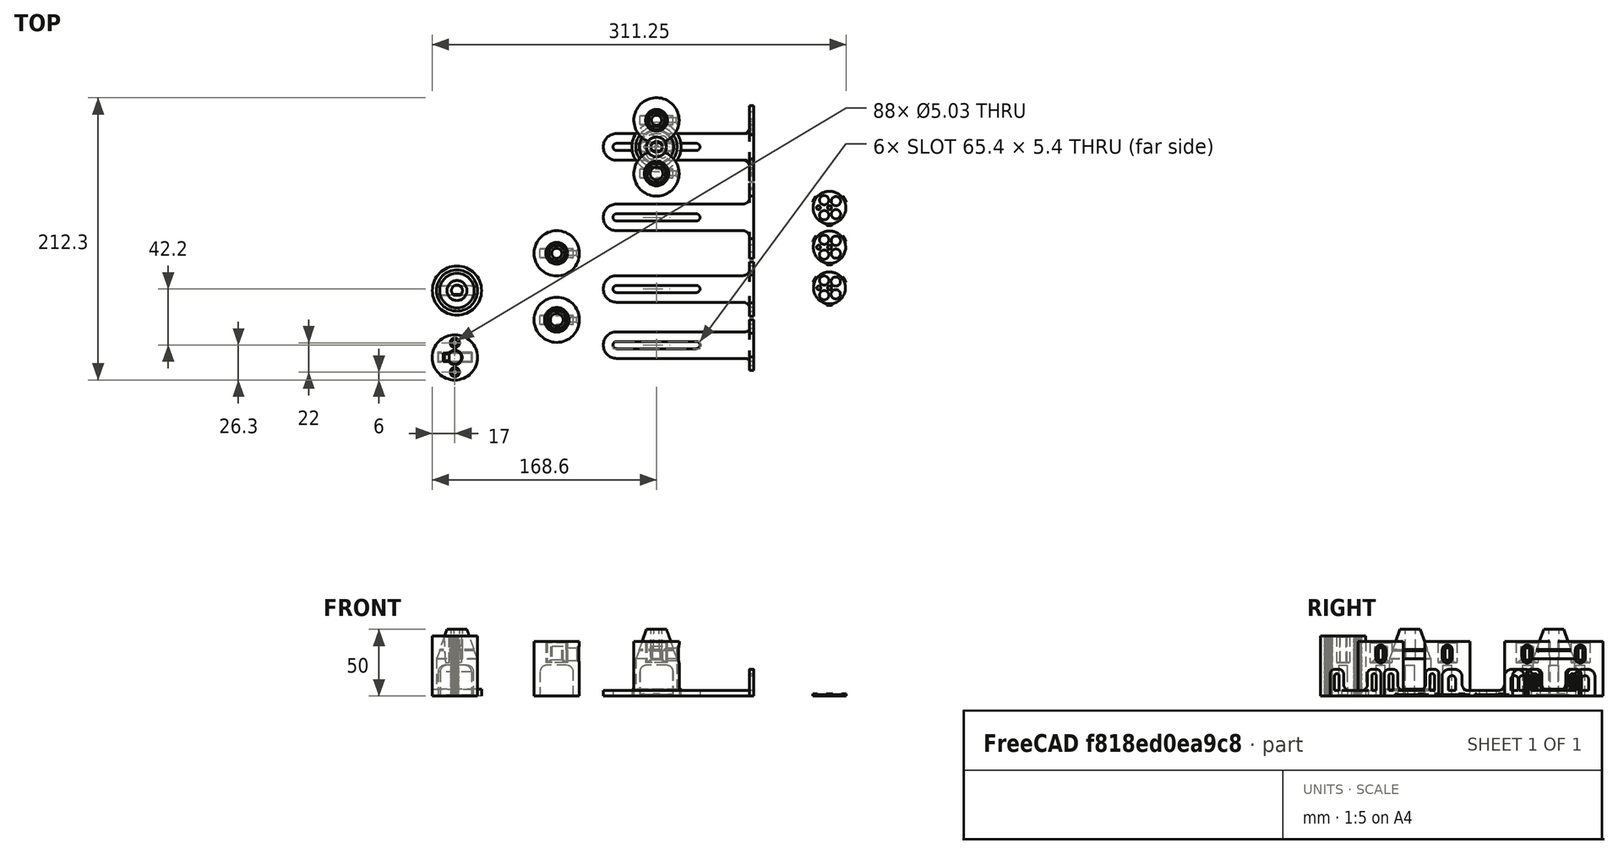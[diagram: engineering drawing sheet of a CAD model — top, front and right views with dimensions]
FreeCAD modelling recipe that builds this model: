
FCSTD DOCUMENT  (FreeCAD 1.0R39285 (Git))
Label: Scherenheberwellenkupplungsadapter
License: All rights reserved
LicenseURL: https://en.wikipedia.org/wiki/All_rights_reserved
objects: Sketcher::SketchObject×41, PartDesign::Pad×23, Part::Feature×12, Mesh::Feature×12, PartDesign::Body×11, PartDesign::Pocket×7, PartDesign::Chamfer×5, App::DocumentObjectGroup×4, PartDesign::AdditiveLoft×3, PartDesign::Plane×2, Measure::MeasureDistance×1, PartDesign::SubtractiveLoft×1, PartDesign::Hole×1
note: 227 computed .brp shape members not serialized (recipe doc carries the construction recipe); baked Part::Feature solids carry a one-line shape summary decoded from their .brp

FEATURE [Sketcher::SketchObject] Sketch  label="Sk-Kupplungszylinder 8x14"
  ArcFitTolerance = 1e-06
  AttachmentSupport = -> [XY_Plane]
  FullyConstrained = true
  MakeInternals = false
  MapMode = 5
  sketch-geometry (1):
    g0: Circle CenterX=0 CenterY=0 CenterZ=0 NormalX=0 NormalY=0 NormalZ=1 AngleXU=0 Radius=17
  constraints (2):
    c: Diameter(g0) = 34
    c: Coincident(g0,g-1)
FEATURE [PartDesign::Pad] Pad  label="P-Kupplungszylinder 8x14"
  Direction = (0,0,1)
  Length = 25
  Length2 = 10
  Profile = -> Sketch
  ReferenceAxis = -> Sketch [N_Axis]
  Refine = true
  Suppressed = false
  Type = 0
FEATURE [Sketcher::SketchObject] Sketch001  label="Sk-Konus groß 8x14"
  ArcFitTolerance = 1e-06
  AttachmentSupport = -> [Pad]
  FullyConstrained = true
  MakeInternals = false
  MapMode = 5
  Placement = pos=(0,0,25) rot=(0,0,1;0rad)
  sketch-geometry (1):
    g0: Circle CenterX=0 CenterY=0 CenterZ=0 NormalX=0 NormalY=0 NormalZ=1 AngleXU=0 Radius=6
  constraints (2):
    c: Coincident(g0,g-1)
    c: Diameter(g0) = 12
FEATURE [Sketcher::SketchObject] Sketch002  label="Sk-Konus klein 8x14"
  ArcFitTolerance = 1e-06
  AttachmentOffset = pos=(0,0,2) rot=(0,0,1;0rad)
  AttachmentSupport = -> [Pad]
  FullyConstrained = true
  MakeInternals = false
  MapMode = 5
  Placement = pos=(0,0,27) rot=(0,0,1;0rad)
  sketch-geometry (1):
    g0: Circle CenterX=0 CenterY=0 CenterZ=0 NormalX=0 NormalY=0 NormalZ=1 AngleXU=0 Radius=3.8
  constraints (2):
    c: Diameter(g0) = 7.6
    c: Coincident(g0,g-1)
FEATURE [PartDesign::AdditiveLoft] AdditiveLoft  label="P-mit Konus 8x14"
  BaseFeature = -> Pad
  Closed = true
  Profile = -> Sketch001
  Refine = true
  Ruled = true
  Sections = -> [Sketch002]
  Suppressed = false
FEATURE [Sketcher::SketchObject] Sketch003  label="Sk-Innenbolzen 8x14"
  ArcFitTolerance = 1e-06
  AttachmentSupport = -> [AdditiveLoft]
  ExternalGeometry = -> [AdditiveLoft]
  FullyConstrained = true
  MakeInternals = false
  MapMode = 5
  Placement = pos=(0,0,27) rot=(0,0,1;0rad)
  sketch-geometry (1):
    g0: Circle CenterX=0 CenterY=0 CenterZ=0 NormalX=0 NormalY=0 NormalZ=1 AngleXU=0 Radius=3.8
  constraints (2):
    c: Coincident(g0,g-1)
    c: Equal(g-3,g0)
FEATURE [PartDesign::Pad] Pad001  label="P-Innenbolzen 8x14"
  BaseFeature = -> AdditiveLoft
  Direction = (0,0,1)
  Length = 10
  Length2 = 10
  Profile = -> Sketch003
  ReferenceAxis = -> Sketch003 [N_Axis]
  Refine = true
  Suppressed = false
  Type = 0
FEATURE [Sketcher::SketchObject] Sketch004  label="Sk-Kupplungsrohr 8x14"
  ArcFitTolerance = 1e-06
  AttachmentSupport = -> [Pad001]
  ExternalGeometry = -> [Pad001]
  FullyConstrained = true
  MakeInternals = false
  MapMode = 5
  Placement = pos=(0,0,37) rot=(0,0,1;0rad)
  sketch-geometry (2):
    g0: Circle CenterX=0 CenterY=0 CenterZ=0 NormalX=0 NormalY=0 NormalZ=1 AngleXU=0 Radius=17
    g1: Circle CenterX=0 CenterY=0 CenterZ=0 NormalX=0 NormalY=0 NormalZ=1 AngleXU=0 Radius=7.2
  constraints (4):
    c: Coincident(g0,g-1)
    c: Equal(g0,g-3)
    c: Diameter(g1) = 14.4
    c: Coincident(g1,g0)
FEATURE [PartDesign::Pad] Pad002  label="P-Adapterhülle 8x14"
  BaseFeature = -> Pad001
  Direction = (0,0,1)
  Length = 4
  Length2 = 14
  Profile = -> Sketch004
  ReferenceAxis = -> Sketch004 [N_Axis]
  Refine = true
  Suppressed = false
  Type = 4
FEATURE [Sketcher::SketchObject] Sketch005  label="Sk-Spindelnut 8x14"
  ArcFitTolerance = 1e-06
  AttachmentSupport = -> [XZ_Plane]
  FullyConstrained = true
  MakeInternals = false
  MapMode = 5
  Placement = pos=(0,0,0) rot=(1,0,0;1.5708rad)
  sketch-geometry (8):
    g0: LineSegment StartX=-12.5 StartY=0 StartZ=0 EndX=12.5 EndY=0 EndZ=0
    g1: LineSegment StartX=12.5 StartY=0 StartZ=0 EndX=12.5 EndY=18 EndZ=0
    g2: LineSegment StartX=7.5 StartY=23 StartZ=0 EndX=-7.5 EndY=23 EndZ=0
    g3: LineSegment StartX=-12.5 StartY=18 StartZ=0 EndX=-12.5 EndY=0 EndZ=0
    g4: ArcOfCircle CenterX=-7.5 CenterY=18 CenterZ=0 NormalX=0 NormalY=0 NormalZ=1 AngleXU=0 Radius=5 StartAngle=1.5708 EndAngle=3.14159
    g5: GeomPoint [constr] X=-12.5 Y=23 Z=0
    g6: ArcOfCircle CenterX=7.5 CenterY=18 CenterZ=0 NormalX=0 NormalY=0 NormalZ=1 AngleXU=0 Radius=5 StartAngle=1e-16 EndAngle=1.5708
    g7: GeomPoint [constr] X=12.5 Y=23 Z=0
  constraints (19):
    c: Coincident(g0,g1)
    c: Coincident(g3,g0)
    c: Horizontal(g2)
    c: Vertical(g1)
    c: Vertical(g3)
    c: DistanceX(g5,g7) = 25
    c: DistanceY(g1,g7) = 23
    c: PointOnObject(g5,g3)
    c: PointOnObject(g5,g2)
    c: Tangent(g3,g4) = -1.5708
    c: Tangent(g2,g4) = -1.5708
    c: PointOnObject(g7,g2)
    c: PointOnObject(g7,g1)
    c: Tangent(g2,g6) = -1.5708
    c: Tangent(g1,g6) = -1.5708
    c: Equal(g4,g6)
    c: Radius(g4) = 5
    c: Symmetric(g0,g0,g-2)
    c: PointOnObject(g0,g-1)
FEATURE [PartDesign::Pocket] Pocket  label="P-Adapter mit  Nut 8x14"
  BaseFeature = -> Pad002
  Direction = (0,1,-2e-16)
  Length = 6.6
  Length2 = 5
  Midplane = true
  Profile = -> Sketch005
  ReferenceAxis = -> Sketch005 [N_Axis]
  Refine = true
  Suppressed = false
  Type = 0
FEATURE [PartDesign::Plane] DatumPlane  label="DatumPlane 8x14"
  AttachmentSupport = -> [Pocket]
  Length = 61.4891
  MapMode = 6
  Placement = pos=(17,0,41) rot=(0.57735,0.57735,0.57735;2.0944rad)
  ResizeMode = 0
  Width = 77.4891
FEATURE [Sketcher::SketchObject] Sketch006  label="Sk-Kupplungsbohrung 8x14"
  ArcFitTolerance = 1e-06
  AttachmentSupport = -> [DatumPlane]
  FullyConstrained = true
  MakeInternals = false
  MapMode = 5
  Placement = pos=(17,0,41) rot=(0.57735,0.57735,0.57735;2.0944rad)
  sketch-geometry (5):
    g0: LineSegment [constr] StartX=0 StartY=0 StartZ=0 EndX=0 EndY=-6.5 EndZ=0
    g1: ArcOfCircle CenterX=-1e-16 CenterY=-12.5 CenterZ=0 NormalX=0 NormalY=0 NormalZ=1 AngleXU=0 Radius=1.8 StartAngle=3.14159 EndAngle=6.28319
    g2: ArcOfCircle CenterX=0 CenterY=-6.5 CenterZ=0 NormalX=0 NormalY=0 NormalZ=1 AngleXU=0 Radius=1.8 StartAngle=0 EndAngle=3.14159
    g3: LineSegment StartX=-1.8 StartY=-6.5 StartZ=0 EndX=-1.8 EndY=-12.5 EndZ=0
    g4: LineSegment StartX=1.8 StartY=-6.5 StartZ=0 EndX=1.8 EndY=-12.5 EndZ=0
  constraints (12):
    c: Distance(g0) = 6.5
    c: Vertical(g0)
    c: Diameter(g1) = 3.6
    c: Vertical(g3)
    c: Vertical(g4)
    c: Tangent(g3,g2) = -1.5708
    c: Tangent(g4,g1) = 1.5708
    c: Tangent(g3,g1) = -1.5708
    c: Coincident(g2,g0)
    c: Tangent(g4,g2) = 1.5708
    c: Coincident(g0,g-1)
    c: DistanceY(g1,g0) = 6
FEATURE [PartDesign::Pocket] Pocket001  label="P-Scherenheberkupplungsadapter 8x14 roh"
  BaseFeature = -> Pocket
  Direction = (-1,0,0)
  Length = 10
  Length2 = 5
  Profile = -> Sketch006
  ReferenceAxis = -> Sketch006 [N_Axis]
  Refine = true
  Suppressed = false
  Type = 0
FEATURE [PartDesign::Chamfer] Chamfer  label="P-Scherenheberkupplungsadapter 8x14 gefast"
  Angle = 45
  Base = -> Pocket001 [Edge40]
  BaseFeature = -> Pocket001
  ChamferType = 0
  FlipDirection = false
  Refine = true
  Size = 1
  Size2 = 1
  SupportTransform = false
  Suppressed = false
  UseAllEdges = false
FEATURE [PartDesign::Chamfer] Chamfer001  label="P-Scherenheberkupplungsadapter 8x14"
  Angle = 45
  Base = -> Chamfer [Edge8,Edge10,Edge11,Edge12,Edge6,Edge7]
  BaseFeature = -> Chamfer
  ChamferType = 0
  FlipDirection = false
  Refine = true
  Size = 2
  Size2 = 1
  SupportTransform = false
  Suppressed = false
  UseAllEdges = false
FEATURE [PartDesign::Body] Body  label="B-Scherenheberkupplungsadpter-8x14mm"
  AllowCompound = false
  Group = -> [Sketch,Pad,Sketch001,Sketch002,AdditiveLoft,Sketch003,Pad001,Sketch004,Pad002,Sketch005,Pocket,DatumPlane,Sketch006,Pocket001,Chamfer,Chamfer001]
  Origin = -> Origin
  Placement = pos=(-75,-80,0) rot=(0,0,1;0rad)
  Tip = -> Chamfer001
FEATURE [Sketcher::SketchObject] Sketch007  label="Sk-Kupplungszylinder 10x16"
  ArcFitTolerance = 1e-06
  AttachmentSupport = -> [XY_Plane001]
  FullyConstrained = true
  MakeInternals = false
  MapMode = 5
  sketch-geometry (1):
    g0: Circle CenterX=0 CenterY=0 CenterZ=0 NormalX=0 NormalY=0 NormalZ=1 AngleXU=0 Radius=17
  constraints (2):
    c: Diameter(g0) = 34
    c: Coincident(g0,g-1)
FEATURE [PartDesign::Pad] Pad003  label="P-Kupplungszylinder 10x16"
  Direction = (0,0,1)
  Length = 25
  Length2 = 10
  Profile = -> Sketch007
  ReferenceAxis = -> Sketch007 [N_Axis]
  Refine = true
  Suppressed = false
  Type = 0
FEATURE [Sketcher::SketchObject] Sketch008  label="Sk-Konus groß  10x16"
  ArcFitTolerance = 1e-06
  AttachmentSupport = -> [Pad003]
  FullyConstrained = true
  MakeInternals = false
  MapMode = 5
  Placement = pos=(0,0,25) rot=(0,0,1;0rad)
  sketch-geometry (1):
    g0: Circle CenterX=0 CenterY=0 CenterZ=0 NormalX=0 NormalY=0 NormalZ=1 AngleXU=0 Radius=7
  constraints (2):
    c: Coincident(g0,g-1)
    c: Diameter(g0) = 14
FEATURE [Sketcher::SketchObject] Sketch009  label="Sk-Konus klein 10x16"
  ArcFitTolerance = 1e-06
  AttachmentOffset = pos=(0,0,2) rot=(0,0,1;0rad)
  AttachmentSupport = -> [Pad003]
  FullyConstrained = true
  MakeInternals = false
  MapMode = 5
  Placement = pos=(0,0,27) rot=(0,0,1;0rad)
  sketch-geometry (1):
    g0: Circle CenterX=0 CenterY=0 CenterZ=0 NormalX=0 NormalY=0 NormalZ=1 AngleXU=0 Radius=4.8
  constraints (2):
    c: Diameter(g0) = 9.6
    c: Coincident(g0,g-1)
FEATURE [PartDesign::AdditiveLoft] AdditiveLoft001  label="P-mit Konus  10x16"
  BaseFeature = -> Pad003
  Closed = true
  Profile = -> Sketch008
  Refine = true
  Ruled = true
  Sections = -> [Sketch009]
  Suppressed = false
FEATURE [Sketcher::SketchObject] Sketch010  label="Sk-Innenbolzen 10x16"
  ArcFitTolerance = 1e-06
  AttachmentSupport = -> [AdditiveLoft001]
  ExternalGeometry = -> [AdditiveLoft001]
  FullyConstrained = true
  MakeInternals = false
  MapMode = 5
  Placement = pos=(0,0,27) rot=(0,0,1;0rad)
  sketch-geometry (1):
    g0: Circle CenterX=0 CenterY=0 CenterZ=0 NormalX=0 NormalY=0 NormalZ=1 AngleXU=0 Radius=4.8
  constraints (2):
    c: Coincident(g0,g-1)
    c: Equal(g-3,g0)
FEATURE [PartDesign::Pad] Pad004  label="P-Innenbolzen 10x16"
  BaseFeature = -> AdditiveLoft001
  Direction = (0,0,1)
  Length = 10
  Length2 = 10
  Profile = -> Sketch010
  ReferenceAxis = -> Sketch010 [N_Axis]
  Refine = true
  Suppressed = false
  Type = 0
FEATURE [Sketcher::SketchObject] Sketch011  label="Sk-Kupplungsrohr 10x16"
  ArcFitTolerance = 1e-06
  AttachmentSupport = -> [Pad004]
  ExternalGeometry = -> [Pad004]
  FullyConstrained = true
  MakeInternals = false
  MapMode = 5
  Placement = pos=(0,0,37) rot=(0,0,1;0rad)
  sketch-geometry (2):
    g0: Circle CenterX=0 CenterY=0 CenterZ=0 NormalX=0 NormalY=0 NormalZ=1 AngleXU=0 Radius=17
    g1: Circle CenterX=0 CenterY=0 CenterZ=0 NormalX=0 NormalY=0 NormalZ=1 AngleXU=0 Radius=8.2
  constraints (4):
    c: Coincident(g0,g-1)
    c: Equal(g0,g-3)
    c: Diameter(g1) = 16.4
    c: Coincident(g1,g0)
FEATURE [PartDesign::Pad] Pad005  label="P-Adapterhülle 10x16"
  BaseFeature = -> Pad004
  Direction = (0,0,1)
  Length = 4
  Length2 = 14
  Profile = -> Sketch011
  ReferenceAxis = -> Sketch011 [N_Axis]
  Refine = true
  Suppressed = false
  Type = 4
FEATURE [Sketcher::SketchObject] Sketch012  label="Sk-Spindelnut 10x16"
  ArcFitTolerance = 1e-06
  AttachmentSupport = -> [XZ_Plane001]
  FullyConstrained = true
  MakeInternals = false
  MapMode = 5
  Placement = pos=(0,0,0) rot=(1,0,0;1.5708rad)
  sketch-geometry (8):
    g0: LineSegment StartX=-12.5 StartY=0 StartZ=0 EndX=12.5 EndY=0 EndZ=0
    g1: LineSegment StartX=12.5 StartY=0 StartZ=0 EndX=12.5 EndY=18 EndZ=0
    g2: LineSegment StartX=7.5 StartY=23 StartZ=0 EndX=-7.5 EndY=23 EndZ=0
    g3: LineSegment StartX=-12.5 StartY=18 StartZ=0 EndX=-12.5 EndY=0 EndZ=0
    g4: ArcOfCircle CenterX=-7.5 CenterY=18 CenterZ=0 NormalX=0 NormalY=0 NormalZ=1 AngleXU=0 Radius=5 StartAngle=1.5708 EndAngle=3.14159
    g5: GeomPoint [constr] X=-12.5 Y=23 Z=0
    g6: ArcOfCircle CenterX=7.5 CenterY=18 CenterZ=0 NormalX=0 NormalY=0 NormalZ=1 AngleXU=0 Radius=5 StartAngle=1e-16 EndAngle=1.5708
    g7: GeomPoint [constr] X=12.5 Y=23 Z=0
  constraints (19):
    c: Coincident(g0,g1)
    c: Coincident(g3,g0)
    c: Horizontal(g2)
    c: Vertical(g1)
    c: Vertical(g3)
    c: DistanceX(g5,g7) = 25
    c: DistanceY(g1,g7) = 23
    c: PointOnObject(g5,g3)
    c: PointOnObject(g5,g2)
    c: Tangent(g3,g4) = -1.5708
    c: Tangent(g2,g4) = -1.5708
    c: PointOnObject(g7,g2)
    c: PointOnObject(g7,g1)
    c: Tangent(g2,g6) = -1.5708
    c: Tangent(g1,g6) = -1.5708
    c: Equal(g4,g6)
    c: Radius(g4) = 5
    c: Symmetric(g0,g0,g-2)
    c: PointOnObject(g0,g-1)
FEATURE [PartDesign::Pocket] Pocket002  label="P-Adapter mit  Nut 10x16"
  BaseFeature = -> Pad005
  Direction = (0,1,-2e-16)
  Length = 6.6
  Length2 = 5
  Midplane = true
  Profile = -> Sketch012
  ReferenceAxis = -> Sketch012 [N_Axis]
  Refine = true
  Suppressed = false
  Type = 0
FEATURE [PartDesign::Plane] DatumPlane001  label="DatumPlane 10x16"
  AttachmentSupport = -> [Pocket002]
  Length = 61.4891
  MapMode = 6
  Placement = pos=(17,0,41) rot=(0.57735,0.57735,0.57735;2.0944rad)
  ResizeMode = 0
  Width = 77.4891
FEATURE [Sketcher::SketchObject] Sketch013  label="Sk-Kupplungsbohrung 10x16"
  ArcFitTolerance = 1e-06
  AttachmentSupport = -> [DatumPlane001]
  FullyConstrained = true
  MakeInternals = false
  MapMode = 5
  Placement = pos=(17,0,41) rot=(0.57735,0.57735,0.57735;2.0944rad)
  sketch-geometry (5):
    g0: LineSegment [constr] StartX=0 StartY=0 StartZ=0 EndX=0 EndY=-6.5 EndZ=0
    g1: ArcOfCircle CenterX=-1e-16 CenterY=-12.5 CenterZ=0 NormalX=0 NormalY=0 NormalZ=1 AngleXU=0 Radius=1.8 StartAngle=3.14159 EndAngle=6.28319
    g2: ArcOfCircle CenterX=0 CenterY=-6.5 CenterZ=0 NormalX=0 NormalY=0 NormalZ=1 AngleXU=0 Radius=1.8 StartAngle=0 EndAngle=3.14159
    g3: LineSegment StartX=-1.8 StartY=-6.5 StartZ=0 EndX=-1.8 EndY=-12.5 EndZ=0
    g4: LineSegment StartX=1.8 StartY=-6.5 StartZ=0 EndX=1.8 EndY=-12.5 EndZ=0
  constraints (12):
    c: Distance(g0) = 6.5
    c: Vertical(g0)
    c: Diameter(g1) = 3.6
    c: Vertical(g3)
    c: Vertical(g4)
    c: Tangent(g3,g2) = -1.5708
    c: Tangent(g4,g1) = 1.5708
    c: Tangent(g3,g1) = -1.5708
    c: Coincident(g2,g0)
    c: Tangent(g4,g2) = 1.5708
    c: Coincident(g0,g-1)
    c: DistanceY(g1,g0) = 6
FEATURE [PartDesign::Pocket] Pocket003  label="P-Scherenheberkupplungsadapter  10x16 roh"
  BaseFeature = -> Pocket002
  Direction = (-1,0,0)
  Length = 10
  Length2 = 5
  Profile = -> Sketch013
  ReferenceAxis = -> Sketch013 [N_Axis]
  Refine = true
  Suppressed = false
  Type = 0
FEATURE [PartDesign::Chamfer] Chamfer002  label="P-Scherenheberkupplungsadapter 10x16 gefast"
  Angle = 45
  Base = -> Pocket003 [Edge36]
  BaseFeature = -> Pocket003
  ChamferType = 0
  FlipDirection = false
  Refine = true
  Size = 1
  Size2 = 1
  SupportTransform = false
  Suppressed = false
  UseAllEdges = false
FEATURE [PartDesign::Chamfer] Chamfer003  label="P-Scherenheberkupplungsadapter 10x16"
  Angle = 45
  Base = -> Chamfer002 [Edge8,Edge10,Edge11,Edge12,Edge6,Edge7]
  BaseFeature = -> Chamfer002
  ChamferType = 0
  FlipDirection = false
  Refine = true
  Size = 2
  Size2 = 1
  SupportTransform = false
  Suppressed = false
  UseAllEdges = false
FEATURE [PartDesign::Body] Body001  label="B-Scherenheberkupplungsadpter-10x16mm"
  AllowCompound = false
  Group = -> [Sketch007,Pad003,Sketch008,Sketch009,AdditiveLoft001,Sketch010,Pad004,Sketch011,Pad005,Sketch012,Pocket002,DatumPlane001,Sketch013,Pocket003,Chamfer002,Chamfer003]
  Origin = -> Origin001
  Placement = pos=(-75,-130,0) rot=(0,0,1;0rad)
  Tip = -> Chamfer003
FEATURE [Part::Feature] Body002  label="S-Scherenheberkupplungsadpter-10x16mm"
  Placement = pos=(0,-20,0) rot=(0,0,1;0rad)
  shape: bbox 34 x 34 x 41 mm, 26 faces (baked)
FEATURE [Part::Feature] Body003  label="S-Scherenheberkupplungsadpter-8x14mm"
  Placement = pos=(0,20,0) rot=(0,0,1;0rad)
  shape: bbox 34 x 34 x 41 mm, 28 faces (baked)
FEATURE [Mesh::Feature] Mesh  label="M-Scherenheberkupplungsadpter-10x16mm"
FEATURE [Mesh::Feature] Mesh001  label="M-Scherenheberkupplungsadpter-08x14mm"
FEATURE [Sketcher::SketchObject] Sketch014  label="B-Montagewinkel NEMA23 - Strebe"
  ArcFitTolerance = 1e-06
  AttachmentSupport = -> [XY_Plane002]
  FullyConstrained = true
  MakeInternals = false
  MapMode = 5
  sketch-geometry (21):
    g0: ArcOfCircle CenterX=-30 CenterY=7.88454e-11 CenterZ=0 NormalX=0 NormalY=0 NormalZ=1 AngleXU=0 Radius=10 StartAngle=1.5708 EndAngle=4.71239
    g1: LineSegment StartX=-30 StartY=-10 StartZ=0 EndX=65 EndY=-10 EndZ=0
    g2: LineSegment StartX=-30 StartY=10 StartZ=0 EndX=65 EndY=10 EndZ=0
    g3: LineSegment [constr] StartX=1.44e-14 StartY=-2.34e-14 StartZ=0 EndX=70 EndY=-2.34e-14 EndZ=0
    g4: LineSegment StartX=70 StartY=-31 StartZ=0 EndX=73 EndY=-31 EndZ=0
    g5: LineSegment StartX=73 StartY=31 StartZ=0 EndX=70 EndY=31 EndZ=0
    g6: LineSegment StartX=73 StartY=-31 StartZ=0 EndX=73 EndY=31 EndZ=0
    g7: LineSegment StartX=70 StartY=31 StartZ=0 EndX=70 EndY=15 EndZ=0
    g8: LineSegment [constr] StartX=70 StartY=10 StartZ=0 EndX=70 EndY=-10 EndZ=0
    g9: LineSegment StartX=70 StartY=-15 StartZ=0 EndX=70 EndY=-31 EndZ=0
    g10: ArcOfCircle CenterX=65 CenterY=15 CenterZ=0 NormalX=0 NormalY=0 NormalZ=1 AngleXU=0 Radius=5 StartAngle=4.71239 EndAngle=6.28319
    g11: GeomPoint [constr] X=70 Y=10 Z=0
    g12: ArcOfCircle CenterX=65 CenterY=-15 CenterZ=0 NormalX=0 NormalY=0 NormalZ=1 AngleXU=0 Radius=5 StartAngle=1.01937e-11 EndAngle=1.5708
    g13: GeomPoint [constr] X=70 Y=-10 Z=0
    g14: LineSegment [constr] StartX=70 StartY=23.55 StartZ=0 EndX=73 EndY=23.55 EndZ=0
    g15: LineSegment [constr] StartX=70 StartY=-23.55 StartZ=0 EndX=73 EndY=-23.55 EndZ=0
    g16: Circle CenterX=-30 CenterY=7.88454e-11 CenterZ=0 NormalX=0 NormalY=0 NormalZ=1 AngleXU=0 Radius=8.28195e-11
    g17: ArcOfCircle CenterX=-30 CenterY=7.88454e-11 CenterZ=0 NormalX=0 NormalY=0 NormalZ=1 AngleXU=0 Radius=2.7 StartAngle=1.5708 EndAngle=4.71239
    g18: ArcOfCircle CenterX=30 CenterY=-4.75e-14 CenterZ=0 NormalX=0 NormalY=0 NormalZ=1 AngleXU=0 Radius=2.7 StartAngle=4.71239 EndAngle=7.85398
    g19: LineSegment StartX=-30 StartY=2.7 StartZ=0 EndX=30 EndY=2.7 EndZ=0
    g20: LineSegment StartX=-30 StartY=-2.7 StartZ=0 EndX=30 EndY=-2.7 EndZ=0
  constraints (53):
    c: Radius(g0) = 10
    c: Horizontal(g2)
    c: Tangent(g1,g0) = -1.5708
    c: Distance(g3) = 70
    c: Coincident(g3,g-1)
    c: Horizontal(g3)
    c: Coincident(g9,g4)
    c: Coincident(g6,g5)
    c: Coincident(g5,g7)
    c: Horizontal(g4)
    c: Horizontal(g5)
    c: DistanceY(g4,g6) = 62
    c: DistanceX(g5,g5) = 3
    c: Coincident(g6,g4)
    c: Symmetric(g4,g5,g-1)
    c: Coincident(g11,g8)
    c: Vertical(g7)
    c: Coincident(g8,g13)
    c: Vertical(g8)
    c: Vertical(g9)
    c: PointOnObject(g3,g8)
    c: Tangent(g2,g0) = 1.5708
    c: Horizontal(g1)
    c: PointOnObject(g11,g2)
    c: PointOnObject(g11,g7)
    c: Tangent(g2,g10) = -1.5708
    c: Tangent(g7,g10) = 1.5708
    c: PointOnObject(g13,g1)
    c: PointOnObject(g13,g9)
    c: Tangent(g1,g12) = 1.5708
    c: Tangent(g9,g12) = 1.5708
    c: Equal(g10,g12)
    c: PointOnObject(g14,g7)
    c: PointOnObject(g14,g6)
    c: Horizontal(g14)
    c: Horizontal(g15)
    c: Symmetric(g15,g14,g-1)
    c: DistanceY(g15,g14) = 47.1
    c: PointOnObject(g15,g9)
    c: Radius(g10) = 5
    c: DistanceX(g0,g3) = 30
    c: Coincident(g16,g0)
    c: Tangent(g16,g-1)
    c: Tangent(g17,g19) = 1.5708
    c: Tangent(g17,g20) = -1.5708
    c: Tangent(g18,g19) = 1.5708
    c: Tangent(g18,g20) = -1.5708
    c: Equal(g17,g18)
    c: Coincident(g17,g0)
    c: PointOnObject(g18,g3)
    c: DistanceX(g3,g18) = 30
    c: Diameter(g17) = 5.4
    c: PointOnObject(g0,g-1)
FEATURE [Measure::MeasureDistance] Distance  label="Distance: 41,00 mm"
  Distance = 41
  DistanceX = 0
  DistanceY = 0
  DistanceZ = 41
  Element1 = -> Body003 [Vertex7]
  Element2 = -> Body003 [Vertex2]
  Position1 = (17,20,41)
  Position2 = (17,20,0)
FEATURE [App::DocumentObjectGroup] Measurements
  Group = -> [Distance]
FEATURE [PartDesign::Pad] Pad006  label="B-Montagewinkel NEMA23 Strebe"
  Direction = (0,0,1)
  Length = 4
  Length2 = 10
  Profile = -> Sketch014
  ReferenceAxis = -> Sketch014 [N_Axis]
  Refine = true
  Suppressed = false
  Type = 0
FEATURE [Sketcher::SketchObject] Sketch015  label="Sk-Montagewinkel NEMA23 Schraubösen"
  ArcFitTolerance = 1e-06
  AttachmentSupport = -> [Pad006]
  ExternalGeometry = -> [Pad006]
  FullyConstrained = true
  MakeInternals = false
  MapMode = 5
  Placement = pos=(73,1.168e-13,0) rot=(0.57735,0.57735,0.57735;2.0944rad)
  sketch-geometry (37):
    g0: LineSegment StartX=-21.4 StartY=20 StartZ=0 EndX=-25.6 EndY=20 EndZ=0
    g1: LineSegment StartX=-31 StartY=14.6 StartZ=0 EndX=-31 EndY=3.6e-15 EndZ=0
    g2: LineSegment StartX=31 StartY=-3.4e-15 StartZ=0 EndX=31 EndY=14.6 EndZ=0
    g3: LineSegment StartX=25.6 StartY=20 StartZ=0 EndX=21.4 EndY=20 EndZ=0
    g4: ArcOfCircle CenterX=-23.5 CenterY=12.5 CenterZ=0 NormalX=0 NormalY=0 NormalZ=1 AngleXU=0 Radius=2.7 StartAngle=-8e-15 EndAngle=3.14159
    g5: ArcOfCircle CenterX=23.5 CenterY=12.5 CenterZ=0 NormalX=0 NormalY=0 NormalZ=1 AngleXU=0 Radius=2.7 StartAngle=3e-16 EndAngle=3.14159
    g6: LineSegment StartX=-20.8 StartY=3.4e-15 StartZ=0 EndX=-20.8 EndY=12.5 EndZ=0
    g7: LineSegment StartX=-26.2 StartY=3.4e-15 StartZ=0 EndX=-26.2 EndY=12.5 EndZ=0
    g8: LineSegment StartX=20.8 StartY=-3.4e-15 StartZ=0 EndX=20.8 EndY=12.5 EndZ=0
    g9: LineSegment StartX=26.2 StartY=-3.4e-15 StartZ=0 EndX=26.2 EndY=12.5 EndZ=0
    g10: LineSegment StartX=-31 StartY=3.4e-15 StartZ=0 EndX=-26.2 EndY=3.4e-15 EndZ=0
    g11: LineSegment [constr] StartX=-26.2 StartY=3.4e-15 StartZ=0 EndX=-20.8 EndY=3.4e-15 EndZ=0
    g12: LineSegment StartX=-20.8 StartY=3.4e-15 StartZ=0 EndX=-16 EndY=3.4e-15 EndZ=0
    g13: LineSegment StartX=16 StartY=-3.4e-15 StartZ=0 EndX=20.8 EndY=-3.4e-15 EndZ=0
    g14: LineSegment [constr] StartX=20.8 StartY=-3.4e-15 StartZ=0 EndX=26.2 EndY=-3.4e-15 EndZ=0
    g15: LineSegment StartX=26.2 StartY=-3.4e-15 StartZ=0 EndX=31 EndY=-3.4e-15 EndZ=0
    g16: LineSegment [constr] StartX=-23.5 StartY=12.5 StartZ=0 EndX=-23.5 EndY=15.2 EndZ=0
    g17: LineSegment [constr] StartX=-23.5 StartY=15.2 StartZ=0 EndX=-23.5 EndY=20 EndZ=0
    g18: ArcOfCircle CenterX=-25.6 CenterY=14.6 CenterZ=0 NormalX=0 NormalY=0 NormalZ=1 AngleXU=0 Radius=5.4 StartAngle=1.5708 EndAngle=3.14159
    g19: GeomPoint [constr] X=-31 Y=20 Z=0
    g20: ArcOfCircle CenterX=-21.4 CenterY=14.6 CenterZ=0 NormalX=0 NormalY=0 NormalZ=1 AngleXU=0 Radius=5.4 StartAngle=0 EndAngle=1.5708
    g21: GeomPoint [constr] X=-16 Y=20 Z=0
    g22: ArcOfCircle CenterX=21.4 CenterY=14.6 CenterZ=0 NormalX=0 NormalY=0 NormalZ=1 AngleXU=0 Radius=5.4 StartAngle=1.5708 EndAngle=3.14159
    g23: GeomPoint [constr] X=16 Y=20 Z=0
    g24: ArcOfCircle CenterX=25.6 CenterY=14.6 CenterZ=0 NormalX=0 NormalY=0 NormalZ=1 AngleXU=0 Radius=5.4 StartAngle=0 EndAngle=1.5708
    g25: GeomPoint [constr] X=31 Y=20 Z=0
    g26: LineSegment StartX=-16 StartY=3.4e-15 StartZ=0 EndX=-11 EndY=3.4e-15 EndZ=0
    g27: LineSegment StartX=-11 StartY=3.4e-15 StartZ=0 EndX=-11 EndY=4 EndZ=0
    g28: LineSegment StartX=16 StartY=-3.4e-15 StartZ=0 EndX=11 EndY=-3.4e-15 EndZ=0
    g29: LineSegment StartX=11 StartY=-3.4e-15 StartZ=0 EndX=11 EndY=4 EndZ=0
    g30: ArcOfCircle CenterX=-11 CenterY=9 CenterZ=0 NormalX=0 NormalY=0 NormalZ=1 AngleXU=0 Radius=5 StartAngle=3.14159 EndAngle=4.71239
    g31: ArcOfCircle CenterX=11 CenterY=9 CenterZ=0 NormalX=0 NormalY=0 NormalZ=1 AngleXU=0 Radius=5 StartAngle=4.71239 EndAngle=6.28319
    g32: LineSegment [constr] StartX=-16 StartY=3.4e-15 StartZ=0 EndX=-16 EndY=9 EndZ=0
    g33: LineSegment StartX=-16 StartY=9 StartZ=0 EndX=-16 EndY=14.6 EndZ=0
    g34: LineSegment StartX=16 StartY=14.6 StartZ=0 EndX=16 EndY=9 EndZ=0
    g35: LineSegment [constr] StartX=16 StartY=9 StartZ=0 EndX=16 EndY=-3.6e-15 EndZ=0
    g36: LineSegment [constr] StartX=-23.5 StartY=12.5 StartZ=0 EndX=23.5 EndY=12.5 EndZ=0
  constraints (95):
    c: Coincident(g12,g32)
    c: Coincident(g1,g10)
    c: Horizontal(g0)
    c: Vertical(g1)
    c: Distance(g32,g1) = 15
    c: Distance(g10,g19) = 20
    c: Coincident(g35,g13)
    c: Coincident(g15,g2)
    c: Vertical(g2)
    c: Horizontal(g3)
    c: Coincident(g2,g-4)
    c: Coincident(g-3,g10)
    c: Vertical(g7)
    c: Vertical(g9)
    c: Diameter(g4) = 5.4
    c: Equal(g4,g5)
    c: Vertical(g6)
    c: Coincident(g10,g11)
    c: Horizontal(g10)
    c: Coincident(g11,g12)
    c: Horizontal(g11)
    c: Horizontal(g12)
    c: Coincident(g13,g14)
    c: Horizontal(g13)
    c: Coincident(g14,g15)
    c: Horizontal(g14)
    c: Horizontal(g15)
    c: Coincident(g7,g10)
    c: Coincident(g6,g11)
    c: Coincident(g8,g13)
    c: Coincident(g9,g14)
    c: Equal(g10,g12)
    c: Equal(g13,g15)
    c: Vertical(g8)
    c: Tangent(g4,g7) = 1.5708
    c: Tangent(g4,g6) = -1.5708
    c: Tangent(g5,g8) = 1.5708
    c: Tangent(g5,g9) = -1.5708
    c: Coincident(g16,g4)
    c: PointOnObject(g16,g4)
    c: Vertical(g16)
    c: Coincident(g17,g16)
    c: Symmetric(g21,g19,g17)
    c: Equal(g17,g10)
    c: PointOnObject(g19,g1)
    c: PointOnObject(g19,g0)
    c: Tangent(g1,g18) = -1.5708
    c: Tangent(g0,g18) = -1.5708
    c: PointOnObject(g21,g0)
    c: Tangent(g0,g20) = -1.5708
    c: PointOnObject(g23,g3)
    c: Tangent(g3,g22) = -1.5708
    c: PointOnObject(g25,g3)
    c: PointOnObject(g25,g2)
    c: Tangent(g3,g24) = -1.5708
    c: Tangent(g2,g24) = -1.5708
    c: Equal(g18,g20)
    c: Equal(g20,g22)
    c: Equal(g22,g24)
    c: Equal(g6,g8)
    c: Equal(g0,g3)
    c: Radius(g18) = 5.4
    c: Coincident(g26,g32)
    c: Coincident(g27,g26)
    c: Vertical(g27)
    c: Coincident(g28,g35)
    c: Coincident(g29,g28)
    c: Vertical(g29)
    c: Equal(g26,g28)
    c: Horizontal(g28)
    c: Horizontal(g26)
    c: PointOnObject(g27,g-5)
    c: PointOnObject(g29,g-5)
    c: Coincident(g30,g27)
    c: Coincident(g31,g29)
    c: Coincident(g32,g33)
    c: Vertical(g32)
    c: Vertical(g33)
    c: PointOnObject(g21,g32)
    c: Vertical(g34)
    c: Vertical(g35)
    c: PointOnObject(g23,g34)
    c: Coincident(g32,g30)
    c: Tangent(g30,g33)
    c: Perpendicular(g30,g27)
    c: Tangent(g34,g31) = 1.5708
    c: Perpendicular(g31,g29)
    c: Coincident(g35,g31)
    c: Equal(g33,g34)
    c: Radius(g30) = 5
    c: Tangent(g33,g20) = -1.5708
    c: Tangent(g34,g22) = -1.5708
    c: Coincident(g36,g4)
    c: Coincident(g36,g5)
    c: DistanceX(g36,g36) = 47
FEATURE [PartDesign::Pad] Pad007  label="P-Montagewinkel NEMA23"
  BaseFeature = -> Pad006
  Direction = (1,1.4e-15,1e-16)
  Length = 3
  Length2 = 10
  Profile = -> Sketch015
  ReferenceAxis = -> Sketch015 [N_Axis]
  Refine = true
  Reversed = true
  Suppressed = false
  Type = 0
FEATURE [PartDesign::Body] Body004  label="B-Montagewinkel NEMA23"
  AllowCompound = false
  Group = -> [Sketch014,Pad006,Sketch015,Pad007]
  Origin = -> Origin002
  Placement = pos=(0,-53,0) rot=(0,0,1;0rad)
  Tip = -> Pad007
FEATURE [Sketcher::SketchObject] Sketch016  label="B-Montagewinkel NEMA17 - Strebe"
  ArcFitTolerance = 1e-06
  AttachmentSupport = -> [XY_Plane003]
  FullyConstrained = true
  MakeInternals = false
  MapMode = 5
  sketch-geometry (20):
    g0: ArcOfCircle CenterX=-30 CenterY=0 CenterZ=0 NormalX=0 NormalY=0 NormalZ=1 AngleXU=0 Radius=10 StartAngle=1.5708 EndAngle=4.71239
    g1: LineSegment StartX=-30 StartY=-10 StartZ=0 EndX=65 EndY=-10 EndZ=0
    g2: LineSegment StartX=-30 StartY=10 StartZ=0 EndX=65 EndY=10 EndZ=0
    g3: LineSegment [constr] StartX=0 StartY=0 StartZ=0 EndX=70 EndY=0 EndZ=0
    g4: LineSegment StartX=70 StartY=-20.5 StartZ=0 EndX=73 EndY=-20.5 EndZ=0
    g5: LineSegment StartX=73 StartY=20.5 StartZ=0 EndX=70 EndY=20.5 EndZ=0
    g6: LineSegment StartX=73 StartY=-20.5 StartZ=0 EndX=73 EndY=20.5 EndZ=0
    g7: LineSegment StartX=70 StartY=20.5 StartZ=0 EndX=70 EndY=15 EndZ=0
    g8: LineSegment [constr] StartX=70 StartY=10 StartZ=0 EndX=70 EndY=-10 EndZ=0
    g9: LineSegment StartX=70 StartY=-15 StartZ=0 EndX=70 EndY=-20.5 EndZ=0
    g10: ArcOfCircle CenterX=65 CenterY=15 CenterZ=0 NormalX=0 NormalY=0 NormalZ=1 AngleXU=0 Radius=5 StartAngle=4.71239 EndAngle=6.28319
    g11: GeomPoint [constr] X=70 Y=10 Z=0
    g12: ArcOfCircle CenterX=65 CenterY=-15 CenterZ=0 NormalX=0 NormalY=0 NormalZ=1 AngleXU=0 Radius=5 StartAngle=0 EndAngle=1.5708
    g13: GeomPoint [constr] X=70 Y=-10 Z=0
    g14: LineSegment [constr] StartX=70 StartY=15.5 StartZ=0 EndX=73 EndY=15.5 EndZ=0
    g15: LineSegment [constr] StartX=70 StartY=-15.5 StartZ=0 EndX=73 EndY=-15.5 EndZ=0
    g16: ArcOfCircle CenterX=-30 CenterY=0 CenterZ=0 NormalX=0 NormalY=0 NormalZ=1 AngleXU=0 Radius=2.7 StartAngle=1.5708 EndAngle=4.71239
    g17: ArcOfCircle CenterX=30 CenterY=0 CenterZ=0 NormalX=0 NormalY=0 NormalZ=1 AngleXU=0 Radius=2.7 StartAngle=4.71239 EndAngle=7.85398
    g18: LineSegment StartX=-30 StartY=2.7 StartZ=0 EndX=30 EndY=2.7 EndZ=0
    g19: LineSegment StartX=-30 StartY=-2.7 StartZ=0 EndX=30 EndY=-2.7 EndZ=0
  constraints (51):
    c: Radius(g0) = 10
    c: Horizontal(g2)
    c: Tangent(g1,g0) = -1.5708
    c: Distance(g3) = 70
    c: Coincident(g3,g-1)
    c: Horizontal(g3)
    c: Coincident(g9,g4)
    c: Coincident(g6,g5)
    c: Coincident(g5,g7)
    c: Horizontal(g4)
    c: Horizontal(g5)
    c: DistanceY(g4,g6) = 41
    c: DistanceX(g5,g5) = 3
    c: Coincident(g6,g4)
    c: Symmetric(g4,g5,g-1)
    c: Coincident(g11,g8)
    c: Vertical(g7)
    c: Coincident(g8,g13)
    c: Vertical(g8)
    c: Vertical(g9)
    c: PointOnObject(g3,g8)
    c: Tangent(g2,g0) = 1.5708
    c: Horizontal(g1)
    c: PointOnObject(g11,g2)
    c: PointOnObject(g11,g7)
    c: Tangent(g2,g10) = -1.5708
    c: Tangent(g7,g10) = 1.5708
    c: PointOnObject(g13,g1)
    c: PointOnObject(g13,g9)
    c: Tangent(g1,g12) = 1.5708
    c: Tangent(g9,g12) = 1.5708
    c: Equal(g10,g12)
    c: PointOnObject(g14,g7)
    c: PointOnObject(g14,g6)
    c: Horizontal(g14)
    c: Horizontal(g15)
    c: Symmetric(g15,g14,g-1)
    c: DistanceY(g15,g14) = 31
    c: PointOnObject(g15,g9)
    c: Radius(g10) = 5
    c: DistanceX(g0,g3) = 30
    c: Tangent(g16,g18) = 1.5708
    c: Tangent(g16,g19) = -1.5708
    c: Tangent(g17,g18) = 1.5708
    c: Tangent(g17,g19) = -1.5708
    c: Equal(g16,g17)
    c: Coincident(g16,g0)
    c: PointOnObject(g17,g3)
    c: DistanceX(g3,g17) = 30
    c: Diameter(g16) = 5.4
    c: PointOnObject(g0,g-1)
FEATURE [PartDesign::Pad] Pad008  label="P-Montagewinkel NEMA17 - Strebe"
  Direction = (0,0,1)
  Length = 4
  Length2 = 10
  Profile = -> Sketch016
  ReferenceAxis = -> Sketch016 [N_Axis]
  Refine = true
  Suppressed = false
  Type = 0
FEATURE [Sketcher::SketchObject] Sketch017  label="Sk-Montagewinkel NEMA17 Schraubösen"
  ArcFitTolerance = 1e-06
  AttachmentSupport = -> [Pad008]
  ExternalGeometry = -> [Pad008]
  FullyConstrained = true
  MakeInternals = false
  MapMode = 5
  Placement = pos=(73,0,0) rot=(0.57735,0.57735,0.57735;2.0944rad)
  sketch-geometry (37):
    g0: LineSegment StartX=-13.9 StartY=20 StartZ=0 EndX=-17.1 EndY=20 EndZ=0
    g1: LineSegment StartX=-20.5 StartY=16.6 StartZ=0 EndX=-20.5 EndY=0 EndZ=0
    g2: LineSegment StartX=20.5 StartY=0 StartZ=0 EndX=20.5 EndY=16.6 EndZ=0
    g3: LineSegment StartX=17.1 StartY=20 StartZ=0 EndX=13.9 EndY=20 EndZ=0
    g4: ArcOfCircle CenterX=-15.5 CenterY=15 CenterZ=0 NormalX=0 NormalY=0 NormalZ=1 AngleXU=0 Radius=1.7 StartAngle=3e-16 EndAngle=3.14159
    g5: ArcOfCircle CenterX=15.5 CenterY=15 CenterZ=0 NormalX=0 NormalY=0 NormalZ=1 AngleXU=0 Radius=1.7 StartAngle=-9e-16 EndAngle=3.14159
    g6: LineSegment StartX=-13.8 StartY=0 StartZ=0 EndX=-13.8 EndY=15 EndZ=0
    g7: LineSegment StartX=-17.2 StartY=0 StartZ=0 EndX=-17.2 EndY=15 EndZ=0
    g8: LineSegment StartX=13.8 StartY=0 StartZ=0 EndX=13.8 EndY=15 EndZ=0
    g9: LineSegment StartX=17.2 StartY=0 StartZ=0 EndX=17.2 EndY=15 EndZ=0
    g10: LineSegment StartX=-20.5 StartY=0 StartZ=0 EndX=-17.2 EndY=0 EndZ=0
    g11: LineSegment [constr] StartX=-17.2 StartY=0 StartZ=0 EndX=-13.8 EndY=0 EndZ=0
    g12: LineSegment StartX=-13.8 StartY=0 StartZ=0 EndX=-10.5 EndY=0 EndZ=0
    g13: LineSegment StartX=10.5 StartY=0 StartZ=0 EndX=13.8 EndY=0 EndZ=0
    g14: LineSegment [constr] StartX=13.8 StartY=0 StartZ=0 EndX=17.2 EndY=0 EndZ=0
    g15: LineSegment StartX=17.2 StartY=0 StartZ=0 EndX=20.5 EndY=0 EndZ=0
    g16: LineSegment [constr] StartX=-15.5 StartY=15 StartZ=0 EndX=-15.5 EndY=16.7 EndZ=0
    g17: LineSegment [constr] StartX=-15.5 StartY=16.7 StartZ=0 EndX=-15.5 EndY=20 EndZ=0
    g18: ArcOfCircle CenterX=-17.1 CenterY=16.6 CenterZ=0 NormalX=0 NormalY=0 NormalZ=1 AngleXU=0 Radius=3.4 StartAngle=1.5708 EndAngle=3.14159
    g19: GeomPoint [constr] X=-20.5 Y=20 Z=0
    g20: ArcOfCircle CenterX=-13.9 CenterY=16.6 CenterZ=0 NormalX=0 NormalY=0 NormalZ=1 AngleXU=0 Radius=3.4 StartAngle=0 EndAngle=1.5708
    g21: GeomPoint [constr] X=-10.5 Y=20 Z=0
    g22: ArcOfCircle CenterX=13.9 CenterY=16.6 CenterZ=0 NormalX=0 NormalY=0 NormalZ=1 AngleXU=0 Radius=3.4 StartAngle=1.5708 EndAngle=3.14159
    g23: GeomPoint [constr] X=10.5 Y=20 Z=0
    g24: ArcOfCircle CenterX=17.1 CenterY=16.6 CenterZ=0 NormalX=0 NormalY=0 NormalZ=1 AngleXU=0 Radius=3.4 StartAngle=0 EndAngle=1.5708
    g25: GeomPoint [constr] X=20.5 Y=20 Z=0
    g26: LineSegment StartX=-10.5 StartY=0 StartZ=0 EndX=-5.5 EndY=0 EndZ=0
    g27: LineSegment StartX=-5.5 StartY=0 StartZ=0 EndX=-5.5 EndY=4 EndZ=0
    g28: LineSegment StartX=10.5 StartY=0 StartZ=0 EndX=5.5 EndY=0 EndZ=0
    g29: LineSegment StartX=5.5 StartY=0 StartZ=0 EndX=5.5 EndY=4 EndZ=0
    g30: ArcOfCircle CenterX=-5.5 CenterY=9 CenterZ=0 NormalX=0 NormalY=0 NormalZ=1 AngleXU=0 Radius=5 StartAngle=3.14159 EndAngle=4.71239
    g31: ArcOfCircle CenterX=5.5 CenterY=9 CenterZ=0 NormalX=0 NormalY=0 NormalZ=1 AngleXU=0 Radius=5 StartAngle=4.71239 EndAngle=6.28319
    g32: LineSegment [constr] StartX=-10.5 StartY=0 StartZ=0 EndX=-10.5 EndY=9 EndZ=0
    g33: LineSegment StartX=-10.5 StartY=9 StartZ=0 EndX=-10.5 EndY=16.6 EndZ=0
    g34: LineSegment StartX=10.5 StartY=16.6 StartZ=0 EndX=10.5 EndY=9 EndZ=0
    g35: LineSegment [constr] StartX=10.5 StartY=9 StartZ=0 EndX=10.5 EndY=0 EndZ=0
    g36: LineSegment [constr] StartX=-15.5 StartY=15 StartZ=0 EndX=15.5 EndY=15 EndZ=0
  constraints (95):
    c: Coincident(g12,g32)
    c: Coincident(g1,g10)
    c: Horizontal(g0)
    c: Vertical(g1)
    c: Distance(g32,g1) = 10
    c: Distance(g10,g19) = 20
    c: Coincident(g35,g13)
    c: Coincident(g15,g2)
    c: Vertical(g2)
    c: Horizontal(g3)
    c: Vertical(g7)
    c: Vertical(g9)
    c: Diameter(g4) = 3.4
    c: Equal(g4,g5)
    c: Vertical(g6)
    c: Coincident(g10,g11)
    c: Horizontal(g10)
    c: Coincident(g11,g12)
    c: Horizontal(g11)
    c: Horizontal(g12)
    c: Coincident(g13,g14)
    c: Horizontal(g13)
    c: Coincident(g14,g15)
    c: Horizontal(g14)
    c: Horizontal(g15)
    c: Coincident(g7,g10)
    c: Coincident(g6,g11)
    c: Coincident(g8,g13)
    c: Coincident(g9,g14)
    c: Equal(g10,g12)
    c: Equal(g13,g15)
    c: Vertical(g8)
    c: Tangent(g4,g7) = 1.5708
    c: Tangent(g4,g6) = -1.5708
    c: Tangent(g5,g8) = 1.5708
    c: Tangent(g5,g9) = -1.5708
    c: Coincident(g16,g4)
    c: PointOnObject(g16,g4)
    c: Vertical(g16)
    c: Coincident(g17,g16)
    c: Symmetric(g21,g19,g17)
    c: Equal(g17,g10)
    c: PointOnObject(g19,g1)
    c: PointOnObject(g19,g0)
    c: Tangent(g1,g18) = -1.5708
    c: Tangent(g0,g18) = -1.5708
    c: PointOnObject(g21,g0)
    c: Tangent(g0,g20) = -1.5708
    c: PointOnObject(g23,g3)
    c: Tangent(g3,g22) = -1.5708
    c: PointOnObject(g25,g3)
    c: PointOnObject(g25,g2)
    c: Tangent(g3,g24) = -1.5708
    c: Tangent(g2,g24) = -1.5708
    c: Equal(g18,g20)
    c: Equal(g20,g22)
    c: Equal(g22,g24)
    c: Equal(g6,g8)
    c: Equal(g0,g3)
    c: Radius(g18) = 3.4
    c: Coincident(g26,g32)
    c: Coincident(g27,g26)
    c: Vertical(g27)
    c: Coincident(g28,g35)
    c: Coincident(g29,g28)
    c: Vertical(g29)
    c: Equal(g26,g28)
    c: Horizontal(g28)
    c: Horizontal(g26)
    c: Coincident(g30,g27)
    c: Coincident(g31,g29)
    c: Coincident(g32,g33)
    c: Vertical(g32)
    c: Vertical(g33)
    c: PointOnObject(g21,g32)
    c: Vertical(g34)
    c: Vertical(g35)
    c: PointOnObject(g23,g34)
    c: Coincident(g32,g30)
    c: Tangent(g30,g33)
    c: Perpendicular(g30,g27)
    c: Tangent(g34,g31) = 1.5708
    c: Perpendicular(g31,g29)
    c: Coincident(g35,g31)
    c: Equal(g33,g34)
    c: Radius(g30) = 5
    c: Tangent(g33,g20) = -1.5708
    c: Tangent(g34,g22) = -1.5708
    c: Coincident(g36,g4)
    c: Coincident(g36,g5)
    c: DistanceX(g36,g36) = 31
    c: PointOnObject(g29,g-3)
    c: Coincident(g2,g-5)
    c: PointOnObject(g27,g-3)
    c: Coincident(g1,g-4)
FEATURE [PartDesign::Pad] Pad009  label="P-Montagewinkel NEMA17"
  BaseFeature = -> Pad008
  Direction = (1,0,0)
  Length = 3
  Length2 = 10
  Profile = -> Sketch017
  ReferenceAxis = -> Sketch017 [N_Axis]
  Refine = true
  Reversed = true
  Suppressed = false
  Type = 0
FEATURE [PartDesign::Body] Body005  label="B-Montagewinkel NEMA17"
  AllowCompound = false
  Group = -> [Sketch016,Sketch017,Pad008,Pad009]
  Origin = -> Origin003
  Placement = pos=(0,-106.8,0) rot=(0,0,1;0rad)
  Tip = -> Pad009
FEATURE [Part::Feature] Body006  label="S-Montagewinkel NEMA23"
  shape: bbox 113 x 62 x 20 mm, 34 faces (baked)
FEATURE [Part::Feature] Body007  label="S-Montagewinkel NEMA17"
  shape: bbox 113 x 41 x 20 mm, 32 faces (baked)
FEATURE [Mesh::Feature] Mesh002  label="M-Montagewinkel NEMA23"
FEATURE [Mesh::Feature] Mesh003  label="M-Montagewinkel NEMA17"
FEATURE [Sketcher::SketchObject] Sketch018  label="B-Montagewinkel NEMA17-Getrb. - Strebe"
  ArcFitTolerance = 1e-06
  AttachmentSupport = -> [XY_Plane004]
  FullyConstrained = true
  MakeInternals = false
  MapMode = 5
  sketch-geometry (20):
    g0: ArcOfCircle CenterX=-30 CenterY=0 CenterZ=0 NormalX=0 NormalY=0 NormalZ=1 AngleXU=0 Radius=10 StartAngle=1.5708 EndAngle=4.71239
    g1: LineSegment StartX=-30 StartY=-10 StartZ=0 EndX=67 EndY=-10 EndZ=0
    g2: LineSegment StartX=-30 StartY=10 StartZ=0 EndX=67 EndY=10 EndZ=0
    g3: LineSegment [constr] StartX=0 StartY=0 StartZ=0 EndX=70 EndY=0 EndZ=0
    g4: LineSegment StartX=70 StartY=-19 StartZ=0 EndX=73 EndY=-19 EndZ=0
    g5: LineSegment StartX=73 StartY=19 StartZ=0 EndX=70 EndY=19 EndZ=0
    g6: LineSegment StartX=73 StartY=-19 StartZ=0 EndX=73 EndY=19 EndZ=0
    g7: LineSegment StartX=70 StartY=19 StartZ=0 EndX=70 EndY=13 EndZ=0
    g8: LineSegment [constr] StartX=70 StartY=10 StartZ=0 EndX=70 EndY=-10 EndZ=0
    g9: LineSegment StartX=70 StartY=-13 StartZ=0 EndX=70 EndY=-19 EndZ=0
    g10: ArcOfCircle CenterX=67 CenterY=13 CenterZ=0 NormalX=0 NormalY=0 NormalZ=1 AngleXU=0 Radius=3 StartAngle=4.71239 EndAngle=6.28319
    g11: GeomPoint [constr] X=70 Y=10 Z=0
    g12: ArcOfCircle CenterX=67 CenterY=-13 CenterZ=0 NormalX=0 NormalY=0 NormalZ=1 AngleXU=0 Radius=3 StartAngle=0 EndAngle=1.5708
    g13: GeomPoint [constr] X=70 Y=-10 Z=0
    g14: LineSegment [constr] StartX=70 StartY=14 StartZ=0 EndX=73 EndY=14 EndZ=0
    g15: LineSegment [constr] StartX=70 StartY=-14 StartZ=0 EndX=73 EndY=-14 EndZ=0
    g16: ArcOfCircle CenterX=-30 CenterY=0 CenterZ=0 NormalX=0 NormalY=0 NormalZ=1 AngleXU=0 Radius=2.7 StartAngle=1.5708 EndAngle=4.71239
    g17: ArcOfCircle CenterX=30 CenterY=0 CenterZ=0 NormalX=0 NormalY=0 NormalZ=1 AngleXU=0 Radius=2.7 StartAngle=4.71239 EndAngle=7.85398
    g18: LineSegment StartX=-30 StartY=2.7 StartZ=0 EndX=30 EndY=2.7 EndZ=0
    g19: LineSegment StartX=-30 StartY=-2.7 StartZ=0 EndX=30 EndY=-2.7 EndZ=0
  constraints (51):
    c: Radius(g0) = 10
    c: Horizontal(g2)
    c: Tangent(g1,g0) = -1.5708
    c: Distance(g3) = 70
    c: Coincident(g3,g-1)
    c: Horizontal(g3)
    c: Coincident(g9,g4)
    c: Coincident(g6,g5)
    c: Coincident(g5,g7)
    c: Horizontal(g4)
    c: Horizontal(g5)
    c: DistanceY(g4,g6) = 38
    c: DistanceX(g5,g5) = 3
    c: Coincident(g6,g4)
    c: Symmetric(g4,g5,g-1)
    c: Coincident(g11,g8)
    c: Vertical(g7)
    c: Coincident(g8,g13)
    c: Vertical(g8)
    c: Vertical(g9)
    c: PointOnObject(g3,g8)
    c: Tangent(g2,g0) = 1.5708
    c: Horizontal(g1)
    c: PointOnObject(g11,g2)
    c: PointOnObject(g11,g7)
    c: Tangent(g2,g10) = -1.5708
    c: Tangent(g7,g10) = 1.5708
    c: PointOnObject(g13,g1)
    c: PointOnObject(g13,g9)
    c: Tangent(g1,g12) = 1.5708
    c: Tangent(g9,g12) = 1.5708
    c: Equal(g10,g12)
    c: PointOnObject(g14,g7)
    c: PointOnObject(g14,g6)
    c: Horizontal(g14)
    c: Horizontal(g15)
    c: Symmetric(g15,g14,g-1)
    c: DistanceY(g15,g14) = 28
    c: PointOnObject(g15,g9)
    c: Radius(g10) = 3
    c: DistanceX(g0,g3) = 30
    c: Tangent(g16,g18) = 1.5708
    c: Tangent(g16,g19) = -1.5708
    c: Tangent(g17,g18) = 1.5708
    c: Tangent(g17,g19) = -1.5708
    c: Equal(g16,g17)
    c: Coincident(g16,g0)
    c: PointOnObject(g17,g3)
    c: DistanceX(g3,g17) = 30
    c: Diameter(g16) = 5.4
    c: PointOnObject(g0,g-1)
FEATURE [PartDesign::Pad] Pad010  label="P-Montagewinkel NEMA17-Getriebe - Strebe"
  Direction = (0,0,1)
  Length = 4
  Length2 = 10
  Profile = -> Sketch018
  ReferenceAxis = -> Sketch018 [N_Axis]
  Refine = true
  Suppressed = false
  Type = 0
FEATURE [Sketcher::SketchObject] Sketch019  label="Sk-Montagewinkel NEMA17-Getrb. Schraubösen"
  ArcFitTolerance = 1e-06
  AttachmentSupport = -> [Pad010]
  ExternalGeometry = -> [Pad010]
  FullyConstrained = true
  MakeInternals = false
  MapMode = 5
  Placement = pos=(73,0,0) rot=(0.57735,0.57735,0.57735;2.0944rad)
  sketch-geometry (37):
    g0: LineSegment StartX=-12.4 StartY=20 StartZ=0 EndX=-15.6 EndY=20 EndZ=0
    g1: LineSegment StartX=-19 StartY=16.6 StartZ=0 EndX=-19 EndY=0 EndZ=0
    g2: LineSegment StartX=19 StartY=0 StartZ=0 EndX=19 EndY=16.6 EndZ=0
    g3: LineSegment StartX=15.6 StartY=20 StartZ=0 EndX=12.4 EndY=20 EndZ=0
    g4: ArcOfCircle CenterX=-14 CenterY=15 CenterZ=0 NormalX=0 NormalY=0 NormalZ=1 AngleXU=0 Radius=1.7 StartAngle=2e-16 EndAngle=3.14159
    g5: ArcOfCircle CenterX=14 CenterY=15 CenterZ=0 NormalX=0 NormalY=0 NormalZ=1 AngleXU=0 Radius=1.7 StartAngle=0 EndAngle=3.14159
    g6: LineSegment StartX=-12.3 StartY=0 StartZ=0 EndX=-12.3 EndY=15 EndZ=0
    g7: LineSegment StartX=-15.7 StartY=0 StartZ=0 EndX=-15.7 EndY=15 EndZ=0
    g8: LineSegment StartX=12.3 StartY=0 StartZ=0 EndX=12.3 EndY=15 EndZ=0
    g9: LineSegment StartX=15.7 StartY=0 StartZ=0 EndX=15.7 EndY=15 EndZ=0
    g10: LineSegment StartX=-19 StartY=0 StartZ=0 EndX=-15.7 EndY=0 EndZ=0
    g11: LineSegment [constr] StartX=-15.7 StartY=0 StartZ=0 EndX=-12.3 EndY=0 EndZ=0
    g12: LineSegment StartX=-12.3 StartY=0 StartZ=0 EndX=-9 EndY=0 EndZ=0
    g13: LineSegment StartX=9 StartY=0 StartZ=0 EndX=12.3 EndY=0 EndZ=0
    g14: LineSegment [constr] StartX=12.3 StartY=0 StartZ=0 EndX=15.7 EndY=0 EndZ=0
    g15: LineSegment StartX=15.7 StartY=0 StartZ=0 EndX=19 EndY=0 EndZ=0
    g16: LineSegment [constr] StartX=-14 StartY=15 StartZ=0 EndX=-14 EndY=16.7 EndZ=0
    g17: LineSegment [constr] StartX=-14 StartY=16.7 StartZ=0 EndX=-14 EndY=20 EndZ=0
    g18: ArcOfCircle CenterX=-15.6 CenterY=16.6 CenterZ=0 NormalX=0 NormalY=0 NormalZ=1 AngleXU=0 Radius=3.4 StartAngle=1.5708 EndAngle=3.14159
    g19: GeomPoint [constr] X=-19 Y=20 Z=0
    g20: ArcOfCircle CenterX=-12.4 CenterY=16.6 CenterZ=0 NormalX=0 NormalY=0 NormalZ=1 AngleXU=0 Radius=3.4 StartAngle=0 EndAngle=1.5708
    g21: GeomPoint [constr] X=-9 Y=20 Z=0
    g22: ArcOfCircle CenterX=12.4 CenterY=16.6 CenterZ=0 NormalX=0 NormalY=0 NormalZ=1 AngleXU=0 Radius=3.4 StartAngle=1.5708 EndAngle=3.14159
    g23: GeomPoint [constr] X=9 Y=20 Z=0
    g24: ArcOfCircle CenterX=15.6 CenterY=16.6 CenterZ=0 NormalX=0 NormalY=0 NormalZ=1 AngleXU=0 Radius=3.4 StartAngle=0 EndAngle=1.5708
    g25: GeomPoint [constr] X=19 Y=20 Z=0
    g26: LineSegment StartX=-9 StartY=0 StartZ=0 EndX=-4 EndY=0 EndZ=0
    g27: LineSegment StartX=-4 StartY=0 StartZ=0 EndX=-4 EndY=4 EndZ=0
    g28: LineSegment StartX=9 StartY=0 StartZ=0 EndX=4 EndY=0 EndZ=0
    g29: LineSegment StartX=4 StartY=0 StartZ=0 EndX=4 EndY=4 EndZ=0
    g30: ArcOfCircle CenterX=-4 CenterY=9 CenterZ=0 NormalX=0 NormalY=0 NormalZ=1 AngleXU=0 Radius=5 StartAngle=3.14159 EndAngle=4.71239
    g31: ArcOfCircle CenterX=4 CenterY=9 CenterZ=0 NormalX=0 NormalY=0 NormalZ=1 AngleXU=0 Radius=5 StartAngle=4.71239 EndAngle=6.28319
    g32: LineSegment [constr] StartX=-9 StartY=0 StartZ=0 EndX=-9 EndY=9 EndZ=0
    g33: LineSegment StartX=-9 StartY=9 StartZ=0 EndX=-9 EndY=16.6 EndZ=0
    g34: LineSegment StartX=9 StartY=16.6 StartZ=0 EndX=9 EndY=9 EndZ=0
    g35: LineSegment [constr] StartX=9 StartY=9 StartZ=0 EndX=9 EndY=0 EndZ=0
    g36: LineSegment [constr] StartX=-14 StartY=15 StartZ=0 EndX=14 EndY=15 EndZ=0
  constraints (97):
    c: Coincident(g12,g32)
    c: Coincident(g1,g10)
    c: Horizontal(g0)
    c: Vertical(g1)
    c: Distance(g32,g1) = 10
    c: Distance(g10,g19) = 20
    c: Coincident(g35,g13)
    c: Coincident(g15,g2)
    c: Vertical(g2)
    c: Horizontal(g3)
    c: Vertical(g7)
    c: Vertical(g9)
    c: Diameter(g4) = 3.4
    c: Equal(g4,g5)
    c: Vertical(g6)
    c: Coincident(g10,g11)
    c: Horizontal(g10)
    c: Coincident(g11,g12)
    c: Horizontal(g11)
    c: Horizontal(g12)
    c: Coincident(g13,g14)
    c: Horizontal(g13)
    c: Coincident(g14,g15)
    c: Horizontal(g14)
    c: Horizontal(g15)
    c: Coincident(g7,g10)
    c: Coincident(g6,g11)
    c: Coincident(g8,g13)
    c: Coincident(g9,g14)
    c: Equal(g10,g12)
    c: Equal(g13,g15)
    c: Vertical(g8)
    c: Tangent(g4,g7) = 1.5708
    c: Tangent(g4,g6) = -1.5708
    c: Tangent(g5,g8) = 1.5708
    c: Tangent(g5,g9) = -1.5708
    c: Coincident(g16,g4)
    c: PointOnObject(g16,g4)
    c: Vertical(g16)
    c: Coincident(g17,g16)
    c: Symmetric(g21,g19,g17)
    c: Equal(g17,g10)
    c: PointOnObject(g19,g1)
    c: PointOnObject(g19,g0)
    c: Tangent(g1,g18) = -1.5708
    c: Tangent(g0,g18) = -1.5708
    c: PointOnObject(g21,g0)
    c: Tangent(g0,g20) = -1.5708
    c: PointOnObject(g23,g3)
    c: Tangent(g3,g22) = -1.5708
    c: PointOnObject(g25,g3)
    c: PointOnObject(g25,g2)
    c: Tangent(g3,g24) = -1.5708
    c: Tangent(g2,g24) = -1.5708
    c: Equal(g18,g20)
    c: Equal(g20,g22)
    c: Equal(g22,g24)
    c: Equal(g6,g8)
    c: Equal(g0,g3)
    c: Radius(g18) = 3.4
    c: Coincident(g26,g32)
    c: Coincident(g27,g26)
    c: Vertical(g27)
    c: Coincident(g28,g35)
    c: Coincident(g29,g28)
    c: Vertical(g29)
    c: Equal(g26,g28)
    c: Horizontal(g28)
    c: Horizontal(g26)
    c: Coincident(g30,g27)
    c: Coincident(g31,g29)
    c: Coincident(g32,g33)
    c: Vertical(g32)
    c: Vertical(g33)
    c: PointOnObject(g21,g32)
    c: Vertical(g34)
    c: Vertical(g35)
    c: PointOnObject(g23,g34)
    c: Coincident(g32,g30)
    c: Tangent(g30,g33)
    c: Perpendicular(g30,g27)
    c: Tangent(g34,g31) = 1.5708
    c: Perpendicular(g31,g29)
    c: Coincident(g35,g31)
    c: Equal(g33,g34)
    c: Radius(g30) = 5
    c: Tangent(g33,g20) = -1.5708
    c: Tangent(g34,g22) = -1.5708
    c: Coincident(g36,g4)
    c: Coincident(g36,g5)
    c: DistanceX(g36,g36) = 28
    c: PointOnObject(g29,g-3)
    c: PointOnObject(g27,g-3)
    c: PointOnObject(g-3,g1)
    c: PointOnObject(g-3,g2)
    c: PointOnObject(g1,g-1)
    c: PointOnObject(g2,g-1)
FEATURE [PartDesign::Pad] Pad011  label="P-Montagewinkel NEMA17-Getriebe"
  BaseFeature = -> Pad010
  Direction = (1,0,0)
  Length = 3
  Length2 = 10
  Profile = -> Sketch019
  ReferenceAxis = -> Sketch019 [N_Axis]
  Refine = true
  Reversed = true
  Suppressed = false
  Type = 0
FEATURE [PartDesign::Body] Body008  label="B-Montagewinkel NEMA17-Getriebe"
  AllowCompound = false
  Group = -> [Sketch018,Sketch019,Pad010,Pad011]
  Origin = -> Origin004
  Placement = pos=(0,-149,0) rot=(0,0,1;0rad)
  Tip = -> Pad011
FEATURE [Part::Feature] Body009  label="S-Montagewinkel NEMA17-Getriebe"
  shape: bbox 113 x 38 x 20 mm, 32 faces (baked)
FEATURE [Mesh::Feature] Mesh004  label="M-Montagewinkel NEMA17-Getriebe"
FEATURE [Sketcher::SketchObject] Sketch020  label="B-Anreislehre-Hebergelenksbolzen - Fläche"
  ArcFitTolerance = 1e-06
  AttachmentSupport = -> [XY_Plane005]
  FullyConstrained = false
  MakeInternals = false
  MapMode = 5
  sketch-geometry (23):
    g0: Circle CenterX=0 CenterY=0 CenterZ=0 NormalX=0 NormalY=0 NormalZ=1 AngleXU=0 Radius=12
    g1: Circle CenterX=0 CenterY=0 CenterZ=0 NormalX=0 NormalY=0 NormalZ=1 AngleXU=0 Radius=1.5
    g2: Circle CenterX=-8 CenterY=0 CenterZ=0 NormalX=0 NormalY=0 NormalZ=1 AngleXU=0 Radius=1.5
    g3: LineSegment [constr] StartX=-12 StartY=0 StartZ=0 EndX=-8 EndY=0 EndZ=0
    g4: LineSegment [constr] StartX=4.77297 StartY=-4.77297 StartZ=0 EndX=4.77297 EndY=4.77297 EndZ=0
    g5: Circle CenterX=4.77297 CenterY=4.77297 CenterZ=0 NormalX=0 NormalY=0 NormalZ=1 AngleXU=0 Radius=3.5
    g6: Circle CenterX=4.77297 CenterY=-4.77297 CenterZ=0 NormalX=0 NormalY=0 NormalZ=1 AngleXU=0 Radius=3.5
    g7: LineSegment [constr] StartX=0 StartY=0 StartZ=0 EndX=1.06066 EndY=1.06066 EndZ=0
    g8: LineSegment [constr] StartX=1.06066 StartY=1.06066 StartZ=0 EndX=2.2981 EndY=2.2981 EndZ=0
    g9: LineSegment [constr] StartX=2.2981 StartY=2.2981 StartZ=0 EndX=4.77297 EndY=4.77297 EndZ=0
    g10: LineSegment [constr] StartX=0 StartY=0 StartZ=0 EndX=1.06066 EndY=-1.06066 EndZ=0
    g11: LineSegment [constr] StartX=1.06066 StartY=-1.06066 StartZ=0 EndX=2.2981 EndY=-2.2981 EndZ=0
    g12: LineSegment [constr] StartX=2.2981 StartY=-2.2981 StartZ=0 EndX=4.77297 EndY=-4.77297 EndZ=0
    g13: LineSegment [constr] StartX=4.77297 StartY=4.77297 StartZ=0 EndX=7.24784 EndY=7.24784 EndZ=0
    g14: LineSegment [constr] StartX=7.24784 StartY=7.24784 StartZ=0 EndX=8.48528 EndY=8.48528 EndZ=0
    g15: LineSegment [constr] StartX=-3.94704 StartY=-5.49673 StartZ=0 EndX=-3.94704 EndY=5.49673 EndZ=0
    g16: Circle CenterX=-3.94704 CenterY=5.49673 CenterZ=0 NormalX=0 NormalY=0 NormalZ=1 AngleXU=0 Radius=3.5
    g17: Circle CenterX=-3.94704 CenterY=-5.49673 CenterZ=0 NormalX=0 NormalY=0 NormalZ=1 AngleXU=0 Radius=3.5
    g18: LineSegment [constr] StartX=-0.459038 StartY=5.20723 StartZ=0 EndX=-3.94704 EndY=5.49673 EndZ=0
    g19: LineSegment [constr] StartX=4.77297 StartY=4.77297 StartZ=0 EndX=1.28496 EndY=5.06248 EndZ=0
    g20: LineSegment [constr] StartX=1.28496 StartY=5.06248 StartZ=0 EndX=-0.459038 EndY=5.20723 EndZ=0
    g21: LineSegment [constr] StartX=-3.94704 StartY=5.49673 StartZ=0 EndX=-6.28168 EndY=8.10431 EndZ=0
    g22: LineSegment [constr] StartX=-6.28168 StartY=8.10431 StartZ=0 EndX=-7.449 EndY=9.4081 EndZ=0
  constraints (60):
    c: Coincident(g0,g-1)
    c: Coincident(g1,g0)
    c: Diameter(g1) = 3
    c: Diameter(g0) = 24
    c: PointOnObject(g2,g-1)
    c: Equal(g2,g1)
    c: PointOnObject(g3,g0)
    c: Coincident(g3,g2)
    c: Horizontal(g3)
    c: DistanceX(g3,g3) = 4
    c: Diameter(g5) = 7
    c: Coincident(g5,g4)
    c: Coincident(g6,g4)
    c: Equal(g5,g6)
    c: Coincident(g7,g0)
    c: PointOnObject(g7,g1)
    c: Coincident(g8,g7)
    c: PointOnObject(g8,g5)
    c: Coincident(g9,g8)
    c: Coincident(g9,g4)
    c: Parallel(g7,g8)
    c: Parallel(g8,g9)
    c: Coincident(g10,g0)
    c: PointOnObject(g10,g1)
    c: Coincident(g11,g10)
    c: Coincident(g12,g11)
    c: Coincident(g12,g4)
    c: PointOnObject(g11,g6)
    c: Parallel(g10,g11)
    c: Parallel(g11,g12)
    c: Symmetric(g4,g4,g-1)
    c: Coincident(g13,g4)
    c: PointOnObject(g13,g5)
    c: Coincident(g14,g13)
    c: PointOnObject(g14,g0)
    c: Parallel(g9,g13)
    c: Parallel(g13,g14)
    c: Equal(g8,g14)
    c: Coincident(g19,g4)
    c: Coincident(g15,g18)
    c: Coincident(g16,g18)
    c: Coincident(g20,g18)
    c: Coincident(g19,g20)
    c: PointOnObject(g19,g5)
    c: PointOnObject(g18,g16)
    c: Equal(g20,g8)
    c: Diameter(g16) = 7
    c: Equal(g16,g17)
    c: Perpendicular(g7,g10)
    c: Parallel(g18,g20)
    c: Parallel(g20,g19)
    c: Coincident(g21,g15)
    c: PointOnObject(g21,g16)
    c: Coincident(g22,g21)
    c: PointOnObject(g22,g0)
    c: Parallel(g22,g21)
    c: Equal(g22,g14)
    c: Symmetric(g15,g15,g-1)
    c: Coincident(g17,g15)
    c: Distance(g14) = 1.75
FEATURE [PartDesign::Pad] Pad012  label="P-Anreislehre-Hebergelenksbolzen Lehre"
  Direction = (0,0,1)
  Length = 1
  Length2 = 10
  Profile = -> Sketch020
  ReferenceAxis = -> Sketch020 [N_Axis]
  Refine = true
  Suppressed = false
  Type = 0
FEATURE [Sketcher::SketchObject] Sketch021  label="Sk-Anreislehre-Hebergelenksbolzen Distanzer"
  ArcFitTolerance = 1e-06
  AttachmentSupport = -> [Pad012]
  ExternalGeometry = -> [Pad012]
  FullyConstrained = true
  MakeInternals = false
  MapMode = 5
  Placement = pos=(0,0,0) rot=(1,0,0;3.14159rad)
  sketch-geometry (22):
    g0: LineSegment [constr] StartX=0 StartY=12 StartZ=0 EndX=-10.3923 EndY=-6 EndZ=0
    g1: LineSegment [constr] StartX=-10.3923 StartY=-6 StartZ=0 EndX=10.3923 EndY=-6 EndZ=0
    g2: LineSegment [constr] StartX=10.3923 StartY=-6 StartZ=0 EndX=0 EndY=12 EndZ=0
    g3: Circle [constr] CenterX=0 CenterY=0 CenterZ=0 NormalX=0 NormalY=0 NormalZ=1 AngleXU=0 Radius=12
    g4: ArcOfCircle CenterX=0 CenterY=0 CenterZ=0 NormalX=0 NormalY=0 NormalZ=1 AngleXU=0 Radius=12 StartAngle=1.37878 EndAngle=1.76281
    g5: ArcOfCircle CenterX=0 CenterY=0 CenterZ=0 NormalX=0 NormalY=0 NormalZ=1 AngleXU=0 Radius=13.1 StartAngle=1.37878 EndAngle=1.76281
    g6: ArcOfCircle CenterX=0 CenterY=0 CenterZ=0 NormalX=0 NormalY=0 NormalZ=1 AngleXU=0 Radius=12 StartAngle=5.56757 EndAngle=5.9516
    g7: ArcOfCircle CenterX=0 CenterY=0 CenterZ=0 NormalX=0 NormalY=0 NormalZ=1 AngleXU=0 Radius=13.1 StartAngle=5.56757 EndAngle=5.9516
    g8: ArcOfCircle CenterX=0 CenterY=0 CenterZ=0 NormalX=0 NormalY=0 NormalZ=1 AngleXU=0 Radius=12 StartAngle=3.47317 EndAngle=3.85721
    g9: ArcOfCircle CenterX=0 CenterY=0 CenterZ=0 NormalX=0 NormalY=0 NormalZ=1 AngleXU=0 Radius=13.1 StartAngle=3.47317 EndAngle=3.85721
    g10: LineSegment StartX=-2.29008 StartY=11.7795 StartZ=0 EndX=-2.5 EndY=12.8592 EndZ=0
    g11: LineSegment StartX=2.29008 StartY=11.7795 StartZ=0 EndX=2.5 EndY=12.8592 EndZ=0
    g12: LineSegment StartX=11.3463 StartY=-3.90646 StartZ=0 EndX=12.3864 EndY=-4.26456 EndZ=0
    g13: LineSegment StartX=9.05627 StartY=-7.87299 StartZ=0 EndX=9.88643 EndY=-8.59468 EndZ=0
    g14: LineSegment StartX=-9.05627 StartY=-7.87299 StartZ=0 EndX=-9.88643 EndY=-8.59468 EndZ=0
    g15: LineSegment StartX=-11.3463 StartY=-3.90646 StartZ=0 EndX=-12.3864 EndY=-4.26456 EndZ=0
    g16: LineSegment [constr] StartX=-2.5 StartY=12.8592 StartZ=0 EndX=2.5 EndY=12.8592 EndZ=0
    g17: LineSegment [constr] StartX=-12.3864 StartY=-4.26456 StartZ=0 EndX=-9.88643 EndY=-8.59468 EndZ=0
    g18: LineSegment [constr] StartX=12.3864 StartY=-4.26456 StartZ=0 EndX=9.88643 EndY=-8.59468 EndZ=0
    g19: LineSegment [constr] StartX=-11.3463 StartY=-3.90646 StartZ=0 EndX=-10.3923 EndY=-6 EndZ=0
    g20: LineSegment [constr] StartX=-10.3923 StartY=-6 StartZ=0 EndX=-9.05627 EndY=-7.87299 EndZ=0
    g21: LineSegment [constr] StartX=11.3463 StartY=-3.90646 StartZ=0 EndX=10.3923 EndY=-6 EndZ=0
  constraints (59):
    c: Coincident(g0,g1)
    c: Coincident(g1,g2)
    c: Coincident(g2,g0)
    c: Equal(g0,g1)
    c: Equal(g0,g2)
    c: PointOnObject(g0,g3)
    c: PointOnObject(g1,g3)
    c: PointOnObject(g2,g3)
    c: Coincident(g3,g-1)
    c: PointOnObject(g2,g-3)
    c: PointOnObject(g0,g-2)
    c: Coincident(g4,g3)
    c: PointOnObject(g4,g3)
    c: Coincident(g5,g3)
    c: Coincident(g6,g3)
    c: Coincident(g7,g3)
    c: Coincident(g8,g3)
    c: PointOnObject(g8,g3)
    c: Coincident(g9,g3)
    c: Coincident(g10,g4)
    c: Coincident(g10,g5)
    c: Coincident(g11,g4)
    c: Coincident(g11,g5)
    c: Coincident(g12,g6)
    c: Coincident(g12,g7)
    c: Coincident(g13,g6)
    c: Coincident(g13,g7)
    c: Coincident(g14,g8)
    c: Coincident(g14,g9)
    c: Coincident(g15,g8)
    c: Coincident(g15,g9)
    c: Perpendicular(g9,g15)
    c: Perpendicular(g9,g14)
    c: Perpendicular(g6,g13)
    c: Perpendicular(g7,g12)
    c: Perpendicular(g4,g10)
    c: Perpendicular(g4,g11)
    c: Coincident(g16,g5)
    c: Coincident(g16,g5)
    c: Horizontal(g16)
    c: Distance(g11) = 1.1
    c: Equal(g11,g12)
    c: Equal(g12,g14)
    c: DistanceX(g16,g16) = 5
    c: Equal(g5,g7)
    c: Coincident(g17,g9)
    c: Coincident(g17,g9)
    c: Coincident(g18,g7)
    c: Coincident(g18,g7)
    c: Equal(g16,g18)
    c: Equal(g18,g17)
    c: Coincident(g19,g8)
    c: Coincident(g19,g0)
    c: Coincident(g20,g0)
    c: Coincident(g20,g8)
    c: Equal(g19,g20)
    c: Coincident(g21,g6)
    c: Coincident(g21,g1)
    c: Equal(g21,g20)
FEATURE [PartDesign::Pad] Pad013  label="P-Anreislehre-Hebergelenksbolzen Distanzer"
  BaseFeature = -> Pad012
  Direction = (0,0,-1)
  Length = 1.5
  Length2 = 10
  Profile = -> Sketch021
  ReferenceAxis = -> Sketch021 [N_Axis]
  Refine = true
  Reversed = true
  Suppressed = false
  Type = 0
FEATURE [PartDesign::Body] Body010  label="B-Scherenhebergelenksbolzen-Anreislehre_24.0"
  AllowCompound = false
  Group = -> [Sketch020,Pad012,Sketch021,Pad013]
  Origin = -> Origin005
  Placement = pos=(130,-106,0) rot=(0,0,1;0rad)
  Tip = -> Pad013
FEATURE [Part::Feature] Body011  label="S-Scherenhebergelenksbolzen-Anreislehre"
  shape: bbox 24.77 x 25.1 x 1.5 mm, 26 faces (baked)
FEATURE [Mesh::Feature] Mesh005  label="M-Scherenhebergelenksbolzen-Anreislehre"
FEATURE [Sketcher::SketchObject] Sketch027  label="Sk-Spindelnut 8x7.0"
  ArcFitTolerance = 1e-06
  AttachmentSupport = -> [XZ_Plane006]
  FullyConstrained = true
  MakeInternals = false
  MapMode = 5
  Placement = pos=(0,0,0) rot=(1,0,0;1.5708rad)
  sketch-geometry (8):
    g0: LineSegment StartX=-12.6 StartY=0 StartZ=0 EndX=12.6 EndY=0 EndZ=0
    g1: LineSegment StartX=12.6 StartY=0 StartZ=0 EndX=12.6 EndY=18 EndZ=0
    g2: LineSegment StartX=7.6 StartY=23 StartZ=0 EndX=-7.6 EndY=23 EndZ=0
    g3: LineSegment StartX=-12.6 StartY=18 StartZ=0 EndX=-12.6 EndY=0 EndZ=0
    g4: ArcOfCircle CenterX=-7.6 CenterY=18 CenterZ=0 NormalX=0 NormalY=0 NormalZ=1 AngleXU=0 Radius=5 StartAngle=1.5708 EndAngle=3.14159
    g5: GeomPoint [constr] X=-12.6 Y=23 Z=0
    g6: ArcOfCircle CenterX=7.6 CenterY=18 CenterZ=0 NormalX=0 NormalY=0 NormalZ=1 AngleXU=0 Radius=5 StartAngle=1e-16 EndAngle=1.5708
    g7: GeomPoint [constr] X=12.6 Y=23 Z=0
  constraints (19):
    c: Coincident(g0,g1)
    c: Coincident(g3,g0)
    c: Horizontal(g2)
    c: Vertical(g1)
    c: Vertical(g3)
    c: DistanceX(g5,g7) = 25.2
    c: DistanceY(g1,g7) = 23
    c: PointOnObject(g5,g3)
    c: PointOnObject(g5,g2)
    c: Tangent(g3,g4) = -1.5708
    c: Tangent(g2,g4) = -1.5708
    c: PointOnObject(g7,g2)
    c: PointOnObject(g7,g1)
    c: Tangent(g2,g6) = -1.5708
    c: Tangent(g1,g6) = -1.5708
    c: Equal(g4,g6)
    c: Radius(g4) = 5
    c: Symmetric(g0,g0,g-2)
    c: PointOnObject(g0,g-1)
FEATURE [Sketcher::SketchObject] Sketch031  label="Sk-Hebermuffe 8x7.0"
  ArcFitTolerance = 1e-06
  FullyConstrained = true
  MakeInternals = false
  MapMode = 5
  sketch-geometry (1):
    g0: Circle CenterX=0 CenterY=0 CenterZ=0 NormalX=0 NormalY=0 NormalZ=1 AngleXU=0 Radius=15.5
  constraints (2):
    c: Coincident(g0,g-1)
    c: Diameter(g0) = 31
FEATURE [PartDesign::Pad] Pad014  label="P-Hebermuffe"
  Direction = (0,0,1)
  Length = 28
  Length2 = 10
  Profile = -> Sketch031
  ReferenceAxis = -> Sketch031 [N_Axis]
  Refine = true
  Suppressed = false
  Type = 0
FEATURE [PartDesign::Pocket] Pocket004  label="P-Hebermuffe mit Tasche"
  BaseFeature = -> Pad014
  Direction = (0,1,-2e-16)
  Length = 7.2
  Length2 = 5
  Midplane = true
  Profile = -> Sketch027
  ReferenceAxis = -> Sketch027 [N_Axis]
  Refine = true
  Suppressed = false
  Type = 0
FEATURE [Sketcher::SketchObject] Sketch023  label="Sk-Wellenkonus aussen 8x7.0"
  ArcFitTolerance = 1e-06
  AttachmentOffset = pos=(0,0,22) rot=(0,0,1;0rad)
  AttachmentSupport = -> [Pocket004]
  FullyConstrained = true
  MakeInternals = false
  MapMode = 5
  Placement = pos=(0,0,50) rot=(0,0,1;0rad)
  sketch-geometry (4):
    g0: Circle CenterX=0 CenterY=0 CenterZ=0 NormalX=0 NormalY=0 NormalZ=1 AngleXU=0 Radius=7.5
    g1: ArcOfCircle CenterX=0 CenterY=0 CenterZ=0 NormalX=0 NormalY=0 NormalZ=1 AngleXU=0 Radius=4.15 StartAngle=5.20834 EndAngle=10.4996
    g2: LineSegment StartX=-1.97484 StartY=-3.65 StartZ=0 EndX=1.97484 EndY=-3.65 EndZ=0
    g3: GeomPoint X=0 Y=4.15 Z=0
  constraints (10):
    c: Diameter(g0) = 15
    c: Coincident(g2,g1)
    c: Horizontal(g2)
    c: Diameter(g1) = 8.3
    c: PointOnObject(g3,g1)
    c: Coincident(g1,g0)
    c: Coincident(g0,g-1)
    c: PointOnObject(g3,g-2)
    c: Coincident(g2,g1)
    c: DistanceY(g1,g3) = 7.8
FEATURE [Sketcher::SketchObject] Sketch028  label="Sk-Wellenkonus mitte-aussen 8x7.0"
  ArcFitTolerance = 1e-06
  AttachmentOffset = pos=(0,0,7) rot=(0,0,1;0rad)
  AttachmentSupport = -> [Pocket004]
  FullyConstrained = true
  MakeInternals = false
  MapMode = 5
  Placement = pos=(0,0,35) rot=(0,0,1;0rad)
  sketch-geometry (4):
    g0: Circle CenterX=0 CenterY=0 CenterZ=0 NormalX=0 NormalY=0 NormalZ=1 AngleXU=0 Radius=13
    g1: ArcOfCircle CenterX=0 CenterY=0 CenterZ=0 NormalX=0 NormalY=0 NormalZ=1 AngleXU=0 Radius=4.15 StartAngle=5.3017 EndAngle=10.4063
    g2: LineSegment StartX=-2.30651 StartY=-3.45 StartZ=0 EndX=2.30651 EndY=-3.45 EndZ=0
    g3: GeomPoint X=0 Y=4.15 Z=0
  constraints (10):
    c: Diameter(g0) = 26
    c: Coincident(g2,g1)
    c: Horizontal(g2)
    c: Diameter(g1) = 8.3
    c: PointOnObject(g3,g1)
    c: Coincident(g1,g0)
    c: Coincident(g0,g-1)
    c: PointOnObject(g3,g-2)
    c: Coincident(g2,g1)
    c: DistanceY(g1,g3) = 7.6
FEATURE [Sketcher::SketchObject] Sketch029  label="Sk-Wellenkonus mitte-innen 8x7.0"
  ArcFitTolerance = 1e-06
  AttachmentOffset = pos=(0,0,6) rot=(0,0,1;0rad)
  AttachmentSupport = -> [Pocket004]
  FullyConstrained = true
  MakeInternals = false
  MapMode = 5
  Placement = pos=(0,0,34) rot=(0,0,1;0rad)
  sketch-geometry (4):
    g0: Circle CenterX=0 CenterY=0 CenterZ=0 NormalX=0 NormalY=0 NormalZ=1 AngleXU=0 Radius=13
    g1: ArcOfCircle CenterX=0 CenterY=0 CenterZ=0 NormalX=0 NormalY=0 NormalZ=1 AngleXU=0 Radius=4.15 StartAngle=5.42135 EndAngle=10.2866
    g2: LineSegment StartX=-2.70185 StartY=-3.15 StartZ=0 EndX=2.70185 EndY=-3.15 EndZ=0
    g3: GeomPoint X=0 Y=4.15 Z=0
  constraints (10):
    c: Diameter(g0) = 26
    c: Coincident(g2,g1)
    c: Horizontal(g2)
    c: Diameter(g1) = 8.3
    c: PointOnObject(g3,g1)
    c: Coincident(g1,g0)
    c: Coincident(g0,g-1)
    c: PointOnObject(g3,g-2)
    c: Coincident(g2,g1)
    c: DistanceY(g1,g3) = 7.3
FEATURE [Sketcher::SketchObject] Sketch030  label="Sk-Wellenkonus innen 8x7.0"
  ArcFitTolerance = 1e-06
  AttachmentSupport = -> [Pocket004]
  FullyConstrained = true
  MakeInternals = false
  MapMode = 5
  Placement = pos=(0,0,28) rot=(0,0,1;0rad)
  sketch-geometry (4):
    g0: Circle CenterX=0 CenterY=0 CenterZ=0 NormalX=0 NormalY=0 NormalZ=1 AngleXU=0 Radius=15.5
    g1: ArcOfCircle CenterX=0 CenterY=0 CenterZ=0 NormalX=0 NormalY=0 NormalZ=1 AngleXU=0 Radius=4.15 StartAngle=5.45761 EndAngle=10.2504
    g2: LineSegment StartX=-2.81425 StartY=-3.05 StartZ=0 EndX=2.81425 EndY=-3.05 EndZ=0
    g3: GeomPoint X=0 Y=4.15 Z=0
  constraints (10):
    c: Diameter(g0) = 31
    c: Coincident(g2,g1)
    c: Horizontal(g2)
    c: Diameter(g1) = 8.3
    c: PointOnObject(g3,g1)
    c: Coincident(g1,g0)
    c: Coincident(g0,g-1)
    c: PointOnObject(g3,g-2)
    c: Coincident(g2,g1)
    c: DistanceY(g1,g3) = 7.2
FEATURE [PartDesign::AdditiveLoft] AdditiveLoft002  label="P-Hebermuffe mit Wellenanschluss"
  BaseFeature = -> Pocket004
  Closed = false
  Profile = -> Sketch030
  Refine = true
  Ruled = true
  Sections = -> [Sketch029,Sketch028,Sketch023]
  Suppressed = false
FEATURE [Sketcher::SketchObject] Sketch032  label="Sk-Verstärkungsring"
  ArcFitTolerance = 1e-06
  AttachmentSupport = -> [AdditiveLoft002]
  ExternalGeometry = -> [AdditiveLoft002]
  FullyConstrained = true
  MakeInternals = false
  MapMode = 5
  Placement = pos=(0,0,0) rot=(1,0,0;3.14159rad)
  sketch-geometry (3):
    g0: Circle CenterX=0 CenterY=0 CenterZ=0 NormalX=0 NormalY=0 NormalZ=1 AngleXU=0 Radius=15.5
    g1: Circle CenterX=0 CenterY=0 CenterZ=0 NormalX=0 NormalY=0 NormalZ=1 AngleXU=0 Radius=18.5
    g2: LineSegment [constr] StartX=15.5 StartY=0 StartZ=0 EndX=18.5 EndY=0 EndZ=0
  constraints (8):
    c: Coincident(g0,g-1)
    c: Coincident(g1,g0)
    c: Equal(g-3,g0)
    c: PointOnObject(g2,g0)
    c: PointOnObject(g2,g1)
    c: PointOnObject(g2,g-1)
    c: Horizontal(g2)
    c: DistanceX(g2,g2) = 3
FEATURE [PartDesign::Pad] Pad015  label="P-Scherenheberwellenmuffe-8x7.0mm"
  BaseFeature = -> AdditiveLoft002
  Direction = (0,0,-1)
  Length = 5
  Length2 = 10
  Profile = -> Sketch032
  ReferenceAxis = -> Sketch032 [N_Axis]
  Refine = true
  Reversed = true
  Suppressed = false
  Type = 0
FEATURE [PartDesign::Body] Body012  label="B-Scherenheberwellenmuffe-8x7.0mm"
  AllowCompound = false
  Group = -> [Sketch023,Sketch027,Sketch028,Sketch029,Sketch030,Sketch031,Pad014,Pocket004,AdditiveLoft002,Sketch032,Pad015]
  Origin = -> Origin006
  Placement = pos=(-150,-108,0) rot=(0,0,1;0rad)
  Tip = -> Pad015
FEATURE [Part::Feature] Body013  label="S-Scherenheberwellenmuffe-8x7.0mm"
  shape: bbox 37 x 37 x 50 mm, 22 faces (baked)
FEATURE [Mesh::Feature] Mesh006  label="M-Scherenheberwellenmuffe-8x7.0mm"
FEATURE [Sketcher::SketchObject] Sketch033  label="B-Anreislehre-Hebergelenksbolzen - Fläche001"
  ArcFitTolerance = 1e-06
  AttachmentSupport = -> [XY_Plane007]
  FullyConstrained = false
  MakeInternals = false
  MapMode = 5
  sketch-geometry (23):
    g0: Circle CenterX=0 CenterY=0 CenterZ=0 NormalX=0 NormalY=0 NormalZ=1 AngleXU=0 Radius=12.15
    g1: Circle CenterX=0 CenterY=0 CenterZ=0 NormalX=0 NormalY=0 NormalZ=1 AngleXU=0 Radius=1.5
    g2: Circle CenterX=-8.15 CenterY=0 CenterZ=0 NormalX=0 NormalY=0 NormalZ=1 AngleXU=0 Radius=1.5
    g3: LineSegment [constr] StartX=-12.15 StartY=0 StartZ=0 EndX=-8.15 EndY=0 EndZ=0
    g4: LineSegment [constr] StartX=4.826 StartY=-4.826 StartZ=0 EndX=4.826 EndY=4.826 EndZ=0
    g5: Circle CenterX=4.826 CenterY=4.826 CenterZ=0 NormalX=0 NormalY=0 NormalZ=1 AngleXU=0 Radius=3.5
    g6: Circle CenterX=4.826 CenterY=-4.826 CenterZ=0 NormalX=0 NormalY=0 NormalZ=1 AngleXU=0 Radius=3.5
    g7: LineSegment [constr] StartX=0 StartY=0 StartZ=0 EndX=1.06066 EndY=1.06066 EndZ=0
    g8: LineSegment [constr] StartX=1.06066 StartY=1.06066 StartZ=0 EndX=2.35113 EndY=2.35113 EndZ=0
    g9: LineSegment [constr] StartX=2.35113 StartY=2.35113 StartZ=0 EndX=4.826 EndY=4.826 EndZ=0
    g10: LineSegment [constr] StartX=0 StartY=0 StartZ=0 EndX=1.06066 EndY=-1.06066 EndZ=0
    g11: LineSegment [constr] StartX=1.06066 StartY=-1.06066 StartZ=0 EndX=2.35113 EndY=-2.35113 EndZ=0
    g12: LineSegment [constr] StartX=2.35113 StartY=-2.35113 StartZ=0 EndX=4.826 EndY=-4.826 EndZ=0
    g13: LineSegment [constr] StartX=4.826 StartY=4.826 StartZ=0 EndX=7.30088 EndY=7.30088 EndZ=0
    g14: LineSegment [constr] StartX=7.30088 StartY=7.30088 StartZ=0 EndX=8.59135 EndY=8.59135 EndZ=0
    g15: LineSegment [constr] StartX=-3.96763 StartY=-5.5694 StartZ=0 EndX=-3.96763 EndY=5.5694 EndZ=0
    g16: Circle CenterX=-3.96763 CenterY=5.5694 CenterZ=0 NormalX=0 NormalY=0 NormalZ=1 AngleXU=0 Radius=3.5
    g17: Circle CenterX=-3.96763 CenterY=-5.5694 CenterZ=0 NormalX=0 NormalY=0 NormalZ=1 AngleXU=0 Radius=3.5
    g18: LineSegment [constr] StartX=-0.48007 StartY=5.27457 StartZ=0 EndX=-3.96763 EndY=5.5694 EndZ=0
    g19: LineSegment [constr] StartX=4.826 StartY=4.826 StartZ=0 EndX=1.33844 EndY=5.12083 EndZ=0
    g20: LineSegment [constr] StartX=1.33844 StartY=5.12083 StartZ=0 EndX=-0.48007 EndY=5.27457 EndZ=0
    g21: LineSegment [constr] StartX=-3.96763 StartY=5.5694 StartZ=0 EndX=-6.25629 EndY=8.21742 EndZ=0
    g22: LineSegment [constr] StartX=-6.25629 StartY=8.21742 StartZ=0 EndX=-7.44966 EndY=9.59818 EndZ=0
  constraints (60):
    c: Coincident(g0,g-1)
    c: Coincident(g1,g0)
    c: Diameter(g1) = 3
    c: Diameter(g0) = 24.3
    c: PointOnObject(g2,g-1)
    c: Equal(g2,g1)
    c: PointOnObject(g3,g0)
    c: Coincident(g3,g2)
    c: Horizontal(g3)
    c: DistanceX(g3,g3) = 4
    c: Diameter(g5) = 7
    c: Coincident(g5,g4)
    c: Coincident(g6,g4)
    c: Equal(g5,g6)
    c: Coincident(g7,g0)
    c: PointOnObject(g7,g1)
    c: Coincident(g8,g7)
    c: PointOnObject(g8,g5)
    c: Coincident(g9,g8)
    c: Coincident(g9,g4)
    c: Parallel(g7,g8)
    c: Parallel(g8,g9)
    c: Coincident(g10,g0)
    c: PointOnObject(g10,g1)
    c: Coincident(g11,g10)
    c: Coincident(g12,g11)
    c: Coincident(g12,g4)
    c: PointOnObject(g11,g6)
    c: Parallel(g10,g11)
    c: Parallel(g11,g12)
    c: Symmetric(g4,g4,g-1)
    c: Coincident(g13,g4)
    c: PointOnObject(g13,g5)
    c: Coincident(g14,g13)
    c: PointOnObject(g14,g0)
    c: Parallel(g9,g13)
    c: Parallel(g13,g14)
    c: Equal(g8,g14)
    c: Coincident(g19,g4)
    c: Coincident(g15,g18)
    c: Coincident(g16,g18)
    c: Coincident(g20,g18)
    c: Coincident(g19,g20)
    c: PointOnObject(g19,g5)
    c: PointOnObject(g18,g16)
    c: Equal(g20,g8)
    c: Diameter(g16) = 7
    c: Equal(g16,g17)
    c: Perpendicular(g7,g10)
    c: Parallel(g18,g20)
    c: Parallel(g20,g19)
    c: Coincident(g21,g15)
    c: PointOnObject(g21,g16)
    c: Coincident(g22,g21)
    c: PointOnObject(g22,g0)
    c: Parallel(g22,g21)
    c: Equal(g22,g14)
    c: Symmetric(g15,g15,g-1)
    c: Coincident(g17,g15)
    c: Distance(g14) = 1.825
FEATURE [PartDesign::Pad] Pad016  label="P-Anreislehre-Hebergelenksbolzen Lehre001"
  Direction = (0,0,1)
  Length = 1
  Length2 = 10
  Profile = -> Sketch033
  ReferenceAxis = -> Sketch033 [N_Axis]
  Refine = true
  Suppressed = false
  Type = 0
FEATURE [Sketcher::SketchObject] Sketch034  label="Sk-Anreislehre-Hebergelenksbolzen Distanzer001"
  ArcFitTolerance = 1e-06
  AttachmentSupport = -> [Pad016]
  ExternalGeometry = -> [Pad016]
  FullyConstrained = true
  MakeInternals = false
  MapMode = 5
  Placement = pos=(0,0,0) rot=(1,0,0;3.14159rad)
  sketch-geometry (22):
    g0: LineSegment [constr] StartX=0 StartY=12.15 StartZ=0 EndX=-10.5222 EndY=-6.075 EndZ=0
    g1: LineSegment [constr] StartX=-10.5222 StartY=-6.075 StartZ=0 EndX=10.5222 EndY=-6.075 EndZ=0
    g2: LineSegment [constr] StartX=10.5222 StartY=-6.075 StartZ=0 EndX=0 EndY=12.15 EndZ=0
    g3: Circle [constr] CenterX=0 CenterY=0 CenterZ=0 NormalX=0 NormalY=0 NormalZ=1 AngleXU=0 Radius=12.15
    g4: ArcOfCircle CenterX=0 CenterY=0 CenterZ=0 NormalX=0 NormalY=0 NormalZ=1 AngleXU=0 Radius=12.15 StartAngle=1.38098 EndAngle=1.76061
    g5: ArcOfCircle CenterX=0 CenterY=0 CenterZ=0 NormalX=0 NormalY=0 NormalZ=1 AngleXU=0 Radius=13.25 StartAngle=1.38098 EndAngle=1.76061
    g6: ArcOfCircle CenterX=0 CenterY=0 CenterZ=0 NormalX=0 NormalY=0 NormalZ=1 AngleXU=0 Radius=12.15 StartAngle=5.56977 EndAngle=5.9494
    g7: ArcOfCircle CenterX=0 CenterY=0 CenterZ=0 NormalX=0 NormalY=0 NormalZ=1 AngleXU=0 Radius=13.25 StartAngle=5.56977 EndAngle=5.9494
    g8: ArcOfCircle CenterX=0 CenterY=0 CenterZ=0 NormalX=0 NormalY=0 NormalZ=1 AngleXU=0 Radius=12.15 StartAngle=3.47537 EndAngle=3.85501
    g9: ArcOfCircle CenterX=0 CenterY=0 CenterZ=0 NormalX=0 NormalY=0 NormalZ=1 AngleXU=0 Radius=13.25 StartAngle=3.47537 EndAngle=3.85501
    g10: LineSegment StartX=-2.29245 StartY=11.9318 StartZ=0 EndX=-2.5 EndY=13.012 EndZ=0
    g11: LineSegment StartX=2.29245 StartY=11.9318 StartZ=0 EndX=2.5 EndY=13.012 EndZ=0
    g12: LineSegment StartX=11.4794 StartY=-3.98056 StartZ=0 EndX=12.5187 EndY=-4.34094 EndZ=0
    g13: LineSegment StartX=9.18699 StartY=-7.95121 StartZ=0 EndX=10.0187 EndY=-8.67107 EndZ=0
    g14: LineSegment StartX=-9.18699 StartY=-7.95121 StartZ=0 EndX=-10.0187 EndY=-8.67107 EndZ=0
    g15: LineSegment StartX=-11.4794 StartY=-3.98056 StartZ=0 EndX=-12.5187 EndY=-4.34094 EndZ=0
    g16: LineSegment [constr] StartX=-2.5 StartY=13.012 StartZ=0 EndX=2.5 EndY=13.012 EndZ=0
    g17: LineSegment [constr] StartX=-12.5187 StartY=-4.34094 StartZ=0 EndX=-10.0187 EndY=-8.67107 EndZ=0
    g18: LineSegment [constr] StartX=12.5187 StartY=-4.34094 StartZ=0 EndX=10.0187 EndY=-8.67107 EndZ=0
    g19: LineSegment [constr] StartX=-11.4794 StartY=-3.98056 StartZ=0 EndX=-10.5222 EndY=-6.075 EndZ=0
    g20: LineSegment [constr] StartX=-10.5222 StartY=-6.075 StartZ=0 EndX=-9.18699 EndY=-7.95121 EndZ=0
    g21: LineSegment [constr] StartX=11.4794 StartY=-3.98056 StartZ=0 EndX=10.5222 EndY=-6.075 EndZ=0
  constraints (59):
    c: Coincident(g0,g1)
    c: Coincident(g1,g2)
    c: Coincident(g2,g0)
    c: Equal(g0,g1)
    c: Equal(g0,g2)
    c: PointOnObject(g0,g3)
    c: PointOnObject(g1,g3)
    c: PointOnObject(g2,g3)
    c: Coincident(g3,g-1)
    c: PointOnObject(g2,g-3)
    c: PointOnObject(g0,g-2)
    c: Coincident(g4,g3)
    c: PointOnObject(g4,g3)
    c: Coincident(g5,g3)
    c: Coincident(g6,g3)
    c: Coincident(g7,g3)
    c: Coincident(g8,g3)
    c: PointOnObject(g8,g3)
    c: Coincident(g9,g3)
    c: Coincident(g10,g4)
    c: Coincident(g10,g5)
    c: Coincident(g11,g4)
    c: Coincident(g11,g5)
    c: Coincident(g12,g6)
    c: Coincident(g12,g7)
    c: Coincident(g13,g6)
    c: Coincident(g13,g7)
    c: Coincident(g14,g8)
    c: Coincident(g14,g9)
    c: Coincident(g15,g8)
    c: Coincident(g15,g9)
    c: Perpendicular(g9,g15)
    c: Perpendicular(g9,g14)
    c: Perpendicular(g6,g13)
    c: Perpendicular(g7,g12)
    c: Perpendicular(g4,g10)
    c: Perpendicular(g4,g11)
    c: Coincident(g16,g5)
    c: Coincident(g16,g5)
    c: Horizontal(g16)
    c: Distance(g11) = 1.1
    c: Equal(g11,g12)
    c: Equal(g12,g14)
    c: DistanceX(g16,g16) = 5
    c: Equal(g5,g7)
    c: Coincident(g17,g9)
    c: Coincident(g17,g9)
    c: Coincident(g18,g7)
    c: Coincident(g18,g7)
    c: Equal(g16,g18)
    c: Equal(g18,g17)
    c: Coincident(g19,g8)
    c: Coincident(g19,g0)
    c: Coincident(g20,g0)
    c: Coincident(g20,g8)
    c: Equal(g19,g20)
    c: Coincident(g21,g6)
    c: Coincident(g21,g1)
    c: Equal(g21,g20)
FEATURE [PartDesign::Pad] Pad017  label="P-Anreislehre-Hebergelenksbolzen Distanzer001"
  BaseFeature = -> Pad016
  Direction = (0,0,-1)
  Length = 1.5
  Length2 = 10
  Profile = -> Sketch034
  ReferenceAxis = -> Sketch034 [N_Axis]
  Refine = true
  Reversed = true
  Suppressed = false
  Type = 0
FEATURE [PartDesign::Body] Body014  label="B-Scherenhebergelenksbolzen-Anreislehre_24.3"
  AllowCompound = false
  Group = -> [Sketch033,Pad016,Sketch034,Pad017]
  Origin = -> Origin007
  Placement = pos=(130,-75.4,0) rot=(0,0,1;0rad)
  Tip = -> Pad017
FEATURE [Sketcher::SketchObject] Sketch035  label="B-Anreislehre-Hebergelenksbolzen - Fläche002"
  ArcFitTolerance = 1e-06
  AttachmentSupport = -> [XY_Plane008]
  FullyConstrained = false
  MakeInternals = false
  MapMode = 5
  sketch-geometry (23):
    g0: Circle CenterX=0 CenterY=0 CenterZ=0 NormalX=0 NormalY=0 NormalZ=1 AngleXU=0 Radius=12.3
    g1: Circle CenterX=0 CenterY=0 CenterZ=0 NormalX=0 NormalY=0 NormalZ=1 AngleXU=0 Radius=1.5
    g2: Circle CenterX=-8.3 CenterY=0 CenterZ=0 NormalX=0 NormalY=0 NormalZ=1 AngleXU=0 Radius=1.5
    g3: LineSegment [constr] StartX=-12.3 StartY=0 StartZ=0 EndX=-8.3 EndY=0 EndZ=0
    g4: LineSegment [constr] StartX=4.87904 StartY=-4.87904 StartZ=0 EndX=4.87904 EndY=4.87904 EndZ=0
    g5: Circle CenterX=4.87904 CenterY=4.87904 CenterZ=0 NormalX=0 NormalY=0 NormalZ=1 AngleXU=0 Radius=3.5
    g6: Circle CenterX=4.87904 CenterY=-4.87904 CenterZ=0 NormalX=0 NormalY=0 NormalZ=1 AngleXU=0 Radius=3.5
    g7: LineSegment [constr] StartX=0 StartY=0 StartZ=0 EndX=1.06066 EndY=1.06066 EndZ=0
    g8: LineSegment [constr] StartX=1.06066 StartY=1.06066 StartZ=0 EndX=2.40416 EndY=2.40416 EndZ=0
    g9: LineSegment [constr] StartX=2.40416 StartY=2.40416 StartZ=0 EndX=4.87904 EndY=4.87904 EndZ=0
    g10: LineSegment [constr] StartX=0 StartY=0 StartZ=0 EndX=1.06066 EndY=-1.06066 EndZ=0
    g11: LineSegment [constr] StartX=1.06066 StartY=-1.06066 StartZ=0 EndX=2.40416 EndY=-2.40416 EndZ=0
    g12: LineSegment [constr] StartX=2.40416 StartY=-2.40416 StartZ=0 EndX=4.87904 EndY=-4.87904 EndZ=0
    g13: LineSegment [constr] StartX=4.87904 StartY=4.87904 StartZ=0 EndX=7.35391 EndY=7.35391 EndZ=0
    g14: LineSegment [constr] StartX=7.35391 StartY=7.35391 StartZ=0 EndX=8.69741 EndY=8.69741 EndZ=0
    g15: LineSegment [constr] StartX=-3.98809 StartY=-5.64327 StartZ=0 EndX=-3.98809 EndY=5.64327 EndZ=0
    g16: Circle CenterX=-3.98809 CenterY=5.64327 CenterZ=0 NormalX=0 NormalY=0 NormalZ=1 AngleXU=0 Radius=3.5
    g17: Circle CenterX=-3.98809 CenterY=-5.64327 CenterZ=0 NormalX=0 NormalY=0 NormalZ=1 AngleXU=0 Radius=3.5
    g18: LineSegment [constr] StartX=-0.501018 StartY=5.34273 StartZ=0 EndX=-3.98809 EndY=5.64327 EndZ=0
    g19: LineSegment [constr] StartX=4.87904 StartY=4.87904 StartZ=0 EndX=1.39196 EndY=5.17958 EndZ=0
    g20: LineSegment [constr] StartX=1.39196 StartY=5.17958 StartZ=0 EndX=-0.501018 EndY=5.34273 EndZ=0
    g21: LineSegment [constr] StartX=-3.98809 StartY=5.64327 StartZ=0 EndX=-6.23585 EndY=8.3261 EndZ=0
    g22: LineSegment [constr] StartX=-6.23585 StartY=8.3261 StartZ=0 EndX=-7.45606 EndY=9.78249 EndZ=0
  constraints (60):
    c: Coincident(g0,g-1)
    c: Coincident(g1,g0)
    c: Diameter(g1) = 3
    c: Diameter(g0) = 24.6
    c: PointOnObject(g2,g-1)
    c: Equal(g2,g1)
    c: PointOnObject(g3,g0)
    c: Coincident(g3,g2)
    c: Horizontal(g3)
    c: DistanceX(g3,g3) = 4
    c: Diameter(g5) = 7
    c: Coincident(g5,g4)
    c: Coincident(g6,g4)
    c: Equal(g5,g6)
    c: Coincident(g7,g0)
    c: PointOnObject(g7,g1)
    c: Coincident(g8,g7)
    c: PointOnObject(g8,g5)
    c: Coincident(g9,g8)
    c: Coincident(g9,g4)
    c: Parallel(g7,g8)
    c: Parallel(g8,g9)
    c: Coincident(g10,g0)
    c: PointOnObject(g10,g1)
    c: Coincident(g11,g10)
    c: Coincident(g12,g11)
    c: Coincident(g12,g4)
    c: PointOnObject(g11,g6)
    c: Parallel(g10,g11)
    c: Parallel(g11,g12)
    c: Symmetric(g4,g4,g-1)
    c: Coincident(g13,g4)
    c: PointOnObject(g13,g5)
    c: Coincident(g14,g13)
    c: PointOnObject(g14,g0)
    c: Parallel(g9,g13)
    c: Parallel(g13,g14)
    c: Equal(g8,g14)
    c: Coincident(g19,g4)
    c: Coincident(g15,g18)
    c: Coincident(g16,g18)
    c: Coincident(g20,g18)
    c: Coincident(g19,g20)
    c: PointOnObject(g19,g5)
    c: PointOnObject(g18,g16)
    c: Equal(g20,g8)
    c: Diameter(g16) = 7
    c: Equal(g16,g17)
    c: Perpendicular(g7,g10)
    c: Parallel(g18,g20)
    c: Parallel(g20,g19)
    c: Coincident(g21,g15)
    c: PointOnObject(g21,g16)
    c: Coincident(g22,g21)
    c: PointOnObject(g22,g0)
    c: Parallel(g22,g21)
    c: Equal(g22,g14)
    c: Symmetric(g15,g15,g-1)
    c: Coincident(g17,g15)
    c: Distance(g14) = 1.9
FEATURE [PartDesign::Pad] Pad018  label="P-Anreislehre-Hebergelenksbolzen Lehre002"
  Direction = (0,0,1)
  Length = 1
  Length2 = 10
  Profile = -> Sketch035
  ReferenceAxis = -> Sketch035 [N_Axis]
  Refine = true
  Suppressed = false
  Type = 0
FEATURE [Sketcher::SketchObject] Sketch036  label="Sk-Anreislehre-Hebergelenksbolzen Distanzer002"
  ArcFitTolerance = 1e-06
  AttachmentSupport = -> [Pad018]
  ExternalGeometry = -> [Pad018]
  FullyConstrained = true
  MakeInternals = false
  MapMode = 5
  Placement = pos=(0,0,0) rot=(1,0,0;3.14159rad)
  sketch-geometry (22):
    g0: LineSegment [constr] StartX=0 StartY=12.3 StartZ=0 EndX=-10.6521 EndY=-6.15 EndZ=0
    g1: LineSegment [constr] StartX=-10.6521 StartY=-6.15 StartZ=0 EndX=10.6521 EndY=-6.15 EndZ=0
    g2: LineSegment [constr] StartX=10.6521 StartY=-6.15 StartZ=0 EndX=0 EndY=12.3 EndZ=0
    g3: Circle [constr] CenterX=0 CenterY=0 CenterZ=0 NormalX=0 NormalY=0 NormalZ=1 AngleXU=0 Radius=12.3
    g4: ArcOfCircle CenterX=0 CenterY=0 CenterZ=0 NormalX=0 NormalY=0 NormalZ=1 AngleXU=0 Radius=12.3 StartAngle=1.38313 EndAngle=1.75846
    g5: ArcOfCircle CenterX=0 CenterY=0 CenterZ=0 NormalX=0 NormalY=0 NormalZ=1 AngleXU=0 Radius=13.4 StartAngle=1.38313 EndAngle=1.75846
    g6: ArcOfCircle CenterX=0 CenterY=0 CenterZ=0 NormalX=0 NormalY=0 NormalZ=1 AngleXU=0 Radius=12.3 StartAngle=5.57192 EndAngle=5.94725
    g7: ArcOfCircle CenterX=0 CenterY=0 CenterZ=0 NormalX=0 NormalY=0 NormalZ=1 AngleXU=0 Radius=13.4 StartAngle=5.57192 EndAngle=5.94725
    g8: ArcOfCircle CenterX=0 CenterY=0 CenterZ=0 NormalX=0 NormalY=0 NormalZ=1 AngleXU=0 Radius=12.3 StartAngle=3.47752 EndAngle=3.85286
    g9: ArcOfCircle CenterX=0 CenterY=0 CenterZ=0 NormalX=0 NormalY=0 NormalZ=1 AngleXU=0 Radius=13.4 StartAngle=3.47752 EndAngle=3.85286
    g10: LineSegment StartX=-2.29478 StartY=12.084 StartZ=0 EndX=-2.5 EndY=13.1647 EndZ=0
    g11: LineSegment StartX=2.29478 StartY=12.084 StartZ=0 EndX=2.5 EndY=13.1647 EndZ=0
    g12: LineSegment StartX=11.6125 StartY=-4.05469 StartZ=0 EndX=12.651 EndY=-4.4173 EndZ=0
    g13: LineSegment StartX=9.3177 StartY=-8.02935 StartZ=0 EndX=10.151 EndY=-8.74743 EndZ=0
    g14: LineSegment StartX=-9.3177 StartY=-8.02935 StartZ=0 EndX=-10.151 EndY=-8.74743 EndZ=0
    g15: LineSegment StartX=-11.6125 StartY=-4.05469 StartZ=0 EndX=-12.651 EndY=-4.4173 EndZ=0
    g16: LineSegment [constr] StartX=-2.5 StartY=13.1647 StartZ=0 EndX=2.5 EndY=13.1647 EndZ=0
    g17: LineSegment [constr] StartX=-12.651 StartY=-4.4173 StartZ=0 EndX=-10.151 EndY=-8.74743 EndZ=0
    g18: LineSegment [constr] StartX=12.651 StartY=-4.4173 StartZ=0 EndX=10.151 EndY=-8.74743 EndZ=0
    g19: LineSegment [constr] StartX=-11.6125 StartY=-4.05469 StartZ=0 EndX=-10.6521 EndY=-6.15 EndZ=0
    g20: LineSegment [constr] StartX=-10.6521 StartY=-6.15 StartZ=0 EndX=-9.3177 EndY=-8.02935 EndZ=0
    g21: LineSegment [constr] StartX=11.6125 StartY=-4.05469 StartZ=0 EndX=10.6521 EndY=-6.15 EndZ=0
  constraints (59):
    c: Coincident(g0,g1)
    c: Coincident(g1,g2)
    c: Coincident(g2,g0)
    c: Equal(g0,g1)
    c: Equal(g0,g2)
    c: PointOnObject(g0,g3)
    c: PointOnObject(g1,g3)
    c: PointOnObject(g2,g3)
    c: Coincident(g3,g-1)
    c: PointOnObject(g2,g-3)
    c: PointOnObject(g0,g-2)
    c: Coincident(g4,g3)
    c: PointOnObject(g4,g3)
    c: Coincident(g5,g3)
    c: Coincident(g6,g3)
    c: Coincident(g7,g3)
    c: Coincident(g8,g3)
    c: PointOnObject(g8,g3)
    c: Coincident(g9,g3)
    c: Coincident(g10,g4)
    c: Coincident(g10,g5)
    c: Coincident(g11,g4)
    c: Coincident(g11,g5)
    c: Coincident(g12,g6)
    c: Coincident(g12,g7)
    c: Coincident(g13,g6)
    c: Coincident(g13,g7)
    c: Coincident(g14,g8)
    c: Coincident(g14,g9)
    c: Coincident(g15,g8)
    c: Coincident(g15,g9)
    c: Perpendicular(g9,g15)
    c: Perpendicular(g9,g14)
    c: Perpendicular(g6,g13)
    c: Perpendicular(g7,g12)
    c: Perpendicular(g4,g10)
    c: Perpendicular(g4,g11)
    c: Coincident(g16,g5)
    c: Coincident(g16,g5)
    c: Horizontal(g16)
    c: Distance(g11) = 1.1
    c: Equal(g11,g12)
    c: Equal(g12,g14)
    c: DistanceX(g16,g16) = 5
    c: Equal(g5,g7)
    c: Coincident(g17,g9)
    c: Coincident(g17,g9)
    c: Coincident(g18,g7)
    c: Coincident(g18,g7)
    c: Equal(g16,g18)
    c: Equal(g18,g17)
    c: Coincident(g19,g8)
    c: Coincident(g19,g0)
    c: Coincident(g20,g0)
    c: Coincident(g20,g8)
    c: Equal(g19,g20)
    c: Coincident(g21,g6)
    c: Coincident(g21,g1)
    c: Equal(g21,g20)
FEATURE [PartDesign::Pad] Pad019  label="P-Anreislehre-Hebergelenksbolzen Distanzer002"
  BaseFeature = -> Pad018
  Direction = (0,0,-1)
  Length = 1.5
  Length2 = 10
  Profile = -> Sketch036
  ReferenceAxis = -> Sketch036 [N_Axis]
  Refine = true
  Reversed = true
  Suppressed = false
  Type = 0
FEATURE [PartDesign::Body] Body015  label="B-Scherenhebergelenksbolzen-Anreislehre_24.6"
  AllowCompound = false
  Group = -> [Sketch035,Pad018,Sketch036,Pad019]
  Origin = -> Origin008
  Placement = pos=(130,-45.7,0) rot=(0,0,1;0rad)
  Tip = -> Pad019
FEATURE [Part::Feature] Body016  label="P-Scherenhebergelenksbolzen-Anreislehre_24.0"
  Placement = pos=(130,-106,0) rot=(0,0,1;0rad)
  shape: bbox 24.77 x 25.1 x 1.5 mm, 26 faces (baked)
FEATURE [Part::Feature] Body017  label="P-Scherenhebergelenksbolzen-Anreislehre_24.3"
  Placement = pos=(130,-75.4,0) rot=(0,0,1;0rad)
  shape: bbox 25.04 x 25.4 x 1.5 mm, 26 faces (baked)
FEATURE [Part::Feature] Body018  label="P-Scherenhebergelenksbolzen-Anreislehre_24.6"
  Placement = pos=(130,-45.7,0) rot=(0,0,1;0rad)
  shape: bbox 25.3 x 25.7 x 1.5 mm, 26 faces (baked)
FEATURE [Mesh::Feature] Mesh007  label="M-Scherenhebergelenksbolzen-Anreislehre_24.6"
FEATURE [Mesh::Feature] Mesh008  label="M-Scherenhebergelenksbolzen-Anreislehre_24.0"
FEATURE [Mesh::Feature] Mesh009  label="M-Scherenhebergelenksbolzen-Anreislehre_24.3"
FEATURE [Sketcher::SketchObject] Sketch037  label="Sk-Kupplungszylinder 10x20"
  ArcFitTolerance = 1e-06
  AttachmentSupport = -> [XY_Plane009]
  FullyConstrained = true
  MakeInternals = false
  MapMode = 5
  sketch-geometry (1):
    g0: Circle CenterX=0 CenterY=0 CenterZ=0 NormalX=0 NormalY=0 NormalZ=1 AngleXU=0 Radius=17
  constraints (2):
    c: Diameter(g0) = 34
    c: Coincident(g0,g-1)
FEATURE [PartDesign::Pad] Pad020  label="P-Kupplungszylinder 10x20"
  Direction = (0,0,1)
  Length = 25
  Length2 = 10
  Profile = -> Sketch037
  ReferenceAxis = -> Sketch037 [N_Axis]
  Refine = true
  Suppressed = false
  Type = 0
FEATURE [Sketcher::SketchObject] Sketch041  label="Sk-Kupplungsrohr 10x20"
  ArcFitTolerance = 1e-06
  AttachmentSupport = -> [Pad020]
  FullyConstrained = true
  MakeInternals = false
  MapMode = 5
  Placement = pos=(0,0,25) rot=(0,0,1;0rad)
  sketch-geometry (2):
    g0: Circle CenterX=0 CenterY=0 CenterZ=0 NormalX=0 NormalY=0 NormalZ=1 AngleXU=0 Radius=17
    g1: Circle CenterX=0 CenterY=0 CenterZ=0 NormalX=0 NormalY=0 NormalZ=1 AngleXU=0 Radius=5
  constraints (4):
    c: Coincident(g0,g-1)
    c: Equal(g0,g-3)
    c: Diameter(g1) = 10
    c: Coincident(g1,g0)
FEATURE [PartDesign::Pad] Pad022  label="P-Adapterhülle 10x20"
  BaseFeature = -> Pad020
  Direction = (0,0,1)
  Length = 20
  Length2 = 20
  Profile = -> Sketch041
  ReferenceAxis = -> Sketch041 [N_Axis]
  Refine = true
  Suppressed = false
  Type = 0
FEATURE [Sketcher::SketchObject] Sketch042  label="Sk-Spindelnut 10x20"
  ArcFitTolerance = 1e-06
  AttachmentSupport = -> [XZ_Plane009]
  FullyConstrained = true
  MakeInternals = false
  MapMode = 5
  Placement = pos=(0,0,0) rot=(1,0,0;1.5708rad)
  sketch-geometry (8):
    g0: LineSegment StartX=-12.5 StartY=0 StartZ=0 EndX=12.5 EndY=0 EndZ=0
    g1: LineSegment StartX=12.5 StartY=0 StartZ=0 EndX=12.5 EndY=18 EndZ=0
    g2: LineSegment StartX=7.5 StartY=23 StartZ=0 EndX=-7.5 EndY=23 EndZ=0
    g3: LineSegment StartX=-12.5 StartY=18 StartZ=0 EndX=-12.5 EndY=0 EndZ=0
    g4: ArcOfCircle CenterX=-7.5 CenterY=18 CenterZ=0 NormalX=0 NormalY=0 NormalZ=1 AngleXU=0 Radius=5 StartAngle=1.5708 EndAngle=3.14159
    g5: GeomPoint [constr] X=-12.5 Y=23 Z=0
    g6: ArcOfCircle CenterX=7.5 CenterY=18 CenterZ=0 NormalX=0 NormalY=0 NormalZ=1 AngleXU=0 Radius=5 StartAngle=2e-16 EndAngle=1.5708
    g7: GeomPoint [constr] X=12.5 Y=23 Z=0
  constraints (19):
    c: Coincident(g0,g1)
    c: Coincident(g3,g0)
    c: Horizontal(g2)
    c: Vertical(g1)
    c: Vertical(g3)
    c: DistanceX(g5,g7) = 25
    c: DistanceY(g1,g7) = 23
    c: PointOnObject(g5,g3)
    c: PointOnObject(g5,g2)
    c: Tangent(g3,g4) = -1.5708
    c: Tangent(g2,g4) = -1.5708
    c: PointOnObject(g7,g2)
    c: PointOnObject(g7,g1)
    c: Tangent(g2,g6) = -1.5708
    c: Tangent(g1,g6) = -1.5708
    c: Equal(g4,g6)
    c: Radius(g4) = 5
    c: Symmetric(g0,g0,g-2)
    c: PointOnObject(g0,g-1)
FEATURE [PartDesign::Pocket] Pocket005  label="P-Adapter mit  Nut 10x20"
  BaseFeature = -> Pad022
  Direction = (0,1,-2e-16)
  Length = 6.1
  Length2 = 5
  Midplane = true
  Profile = -> Sketch042
  ReferenceAxis = -> Sketch042 [N_Axis]
  Refine = true
  Suppressed = false
  Type = 0
FEATURE [Sketcher::SketchObject] Sketch044  label="Sk-Keilnut 10x20 oben"
  ArcFitTolerance = 1e-06
  AttachmentSupport = -> [Pocket005]
  ExternalGeometry = -> [Pocket005]
  FullyConstrained = true
  MakeInternals = false
  MapMode = 5
  Placement = pos=(0,0,45) rot=(0,0,1;0rad)
  sketch-geometry (6):
    g0: LineSegment [constr] StartX=5 StartY=0 StartZ=0 EndX=-4.20833 EndY=0 EndZ=0
    g1: LineSegment StartX=-8.20833 StartY=2.7 StartZ=0 EndX=-8.20833 EndY=-2.7 EndZ=0
    g2: LineSegment StartX=-8.20833 StartY=-2.7 StartZ=0 EndX=-4.20833 EndY=-2.7 EndZ=0
    g3: LineSegment StartX=-4.20833 StartY=2.7 StartZ=0 EndX=-8.20833 EndY=2.7 EndZ=0
    g4: LineSegment StartX=-4.20833 StartY=-2.7 StartZ=0 EndX=-4.20833 EndY=0 EndZ=0
    g5: LineSegment StartX=-4.20833 StartY=0 StartZ=0 EndX=-4.20833 EndY=2.7 EndZ=0
  constraints (19):
    c: PointOnObject(g0,g-3)
    c: PointOnObject(g-1,g0)
    c: Horizontal(g0)
    c: DistanceX(g0,g0) = 9.20833
    c: Coincident(g1,g2)
    c: Coincident(g2,g4)
    c: Coincident(g5,g3)
    c: Coincident(g3,g1)
    c: Vertical(g1)
    c: Horizontal(g2)
    c: Horizontal(g3)
    c: PointOnObject(g2,g-3)
    c: Coincident(g4,g5)
    c: Vertical(g4)
    c: Vertical(g5)
    c: Coincident(g4,g0)
    c: Equal(g5,g4)
    c: DistanceY(g1,g1) = 5.4
    c: DistanceX(g3,g3) = 4
FEATURE [Sketcher::SketchObject] Sketch045  label="Sk-Keilnut 10x20 unten"
  ArcFitTolerance = 1e-06
  AttachmentSupport = -> [Pocket005]
  ExternalGeometry = -> [Sketch044]
  FullyConstrained = true
  MakeInternals = false
  MapMode = 5
  Placement = pos=(0,0,25) rot=(0,0,1;0rad)
  sketch-geometry (5):
    g0: LineSegment StartX=-7.20833 StartY=2.7 StartZ=0 EndX=-7.20833 EndY=-2.7 EndZ=0
    g1: LineSegment StartX=-7.20833 StartY=-2.7 StartZ=0 EndX=-4.20833 EndY=-2.7 EndZ=0
    g2: LineSegment StartX=-4.20833 StartY=2.7 StartZ=0 EndX=-7.20833 EndY=2.7 EndZ=0
    g3: LineSegment StartX=-4.20833 StartY=-2.7 StartZ=0 EndX=-4.20833 EndY=0 EndZ=0
    g4: LineSegment StartX=-4.20833 StartY=0 StartZ=0 EndX=-4.20833 EndY=2.7 EndZ=0
  constraints (13):
    c: Coincident(g0,g1)
    c: Coincident(g1,g3)
    c: Coincident(g4,g2)
    c: Coincident(g2,g0)
    c: Vertical(g0)
    c: Horizontal(g1)
    c: Horizontal(g2)
    c: Coincident(g3,g4)
    c: Vertical(g3)
    c: Coincident(g3,g-3)
    c: Coincident(g2,g-3)
    c: DistanceX(g2,g2) = 3
    c: Equal(g4,g3)
FEATURE [PartDesign::SubtractiveLoft] SubtractiveLoft  label="P-Adapter mit Keilnut 10x20"
  BaseFeature = -> Pocket005
  Closed = false
  Profile = -> Sketch044
  Refine = true
  Ruled = false
  Sections = -> [Sketch045]
  Suppressed = false
FEATURE [Sketcher::SketchObject] Sketch046  label="Sk-Strebbohrungen 10x20"
  ArcFitTolerance = 1e-06
  AttachmentSupport = -> [SubtractiveLoft]
  ExternalGeometry = -> [SubtractiveLoft]
  FullyConstrained = false
  MakeInternals = false
  MapMode = 5
  Placement = pos=(0,0,45) rot=(0,0,1;0rad)
  sketch-geometry (7):
    g0: Circle CenterX=0 CenterY=11 CenterZ=0 NormalX=0 NormalY=0 NormalZ=1 AngleXU=0 Radius=3
    g1: Circle CenterX=0 CenterY=-11 CenterZ=0 NormalX=0 NormalY=0 NormalZ=1 AngleXU=0 Radius=3
    g2: LineSegment [constr] StartX=0 StartY=0 StartZ=0 EndX=0 EndY=5 EndZ=0
    g3: LineSegment [constr] StartX=0 StartY=5 StartZ=0 EndX=0 EndY=11 EndZ=0
    g4: LineSegment [constr] StartX=0 StartY=0 StartZ=0 EndX=3.9343e-12 EndY=-5 EndZ=0
    g5: LineSegment [constr] StartX=3.9343e-12 StartY=-5 StartZ=0 EndX=0 EndY=-11 EndZ=0
    g6: LineSegment [constr] StartX=0 StartY=11 StartZ=0 EndX=0 EndY=17 EndZ=0
  constraints (18):
    c: Diameter(g0) = 6
    c: PointOnObject(g1,g-2)
    c: Equal(g0,g1)
    c: Coincident(g2,g-1)
    c: Coincident(g3,g0)
    c: Coincident(g4,g2)
    c: Coincident(g5,g1)
    c: Coincident(g2,g3)
    c: Vertical(g2)
    c: Vertical(g3)
    c: Coincident(g4,g5)
    c: PointOnObject(g2,g-4)
    c: Equal(g2,g4)
    c: Equal(g3,g5)
    c: Coincident(g6,g0)
    c: PointOnObject(g6,g-3)
    c: Vertical(g6)
    c: Equal(g6,g3)
FEATURE [PartDesign::Hole] Hole  label="P-Adapter mit Strebgewinden 10x20"
  BaseFeature = -> SubtractiveLoft
  CustomThreadClearance = 0
  Depth = 133.019
  DepthType = 1
  Diameter = 5.026
  DrillForDepth = false
  DrillPoint = 1
  DrillPointAngle = 118
  HoleCutCountersinkAngle = 90
  HoleCutCustomValues = false
  HoleCutDepth = 0
  HoleCutDiameter = 7
  HoleCutType = 2
  ModelThread = true
  Profile = -> Sketch046
  Refine = true
  Suppressed = false
  Tapered = false
  TaperedAngle = 90
  ThreadClass = 0
  ThreadDepth = 133.019
  ThreadDepthType = 0
  ThreadDirection = 0
  ThreadFit = 0
  ThreadSize = 14
  ThreadType = 1
  Threaded = true
  UseCustomThreadClearance = false
FEATURE [Sketcher::SketchObject] Sketch047  label="Sk-Kupplungskeil Profil 5x4x20"
  ArcFitTolerance = 1e-06
  AttachmentSupport = -> [XZ_Plane010]
  FullyConstrained = true
  MakeInternals = false
  MapMode = 5
  Placement = pos=(0,0,0) rot=(1,0,0;1.5708rad)
  sketch-geometry (4):
    g0: LineSegment StartX=0 StartY=0 StartZ=0 EndX=4 EndY=0 EndZ=0
    g1: LineSegment StartX=4 StartY=0 StartZ=0 EndX=3 EndY=20 EndZ=0
    g2: LineSegment StartX=3 StartY=20 StartZ=0 EndX=0 EndY=20 EndZ=0
    g3: LineSegment StartX=0 StartY=20 StartZ=0 EndX=0 EndY=0 EndZ=0
  constraints (11):
    c: Coincident(g0,g1)
    c: Coincident(g1,g2)
    c: Coincident(g2,g3)
    c: Coincident(g3,g0)
    c: Horizontal(g0)
    c: Horizontal(g2)
    c: Vertical(g3)
    c: Coincident(g0,g-1)
    c: DistanceY(g3,g3) = 20
    c: DistanceX(g0,g0) = 4
    c: DistanceX(g2,g2) = 3
FEATURE [PartDesign::Pad] Pad023  label="P-Kupplungskeil-5x4x20mm"
  Direction = (0,-1,2e-16)
  Length = 5
  Length2 = 10
  Placement = pos=(0,0,0) rot=(1,0,0;1.5708rad)
  Profile = -> Sketch047
  ReferenceAxis = -> Sketch047 [N_Axis]
  Refine = true
  Suppressed = false
  Type = 0
FEATURE [PartDesign::Body] Body021  label="B-Scherenheberwellenkupplungskeil-5x4x20mm"
  AllowCompound = false
  Group = -> [Sketch047,Pad023]
  Origin = -> Origin010
  Placement = pos=(-155.8,-155.8,45.1) rot=(0,1,0;3.14159rad)
  Tip = -> Pad023
FEATURE [Part::Feature] Body022  label="P-Scherenheberwellenkupplungskeil-5x4x20mm"
  Placement = pos=(-155.8,-155.8,45.1) rot=(0,1,0;3.14159rad)
  shape: bbox 4 x 5 x 20 mm, 6 faces (baked)
FEATURE [Mesh::Feature] Mesh011  label="M-Scherenheberwellenkupplungskeil-5x4x20mm"
FEATURE [Sketcher::SketchObject] Sketch048  label="Sk-Spindelnutkeil 10x20"
  ArcFitTolerance = 1e-06
  AttachmentSupport = -> [Pocket005]
  FullyConstrained = true
  MakeInternals = false
  MapMode = 5
  Placement = pos=(12.5,0,0) rot=(0.57735,-0.57735,-0.57735;2.0944rad)
  sketch-geometry (4):
    g0: LineSegment StartX=-3.05 StartY=18 StartZ=0 EndX=-3.25 EndY=0 EndZ=0
    g1: LineSegment StartX=-3.25 StartY=0 StartZ=0 EndX=3.25 EndY=0 EndZ=0
    g2: LineSegment StartX=3.25 StartY=0 StartZ=0 EndX=3.05 EndY=18 EndZ=0
    g3: LineSegment StartX=3.05 StartY=18 StartZ=0 EndX=-3.05 EndY=18 EndZ=0
  constraints (9):
    c: Coincident(g0,g1)
    c: Coincident(g2,g3)
    c: Coincident(g3,g0)
    c: Coincident(g-3,g0)
    c: Coincident(g2,g-3)
    c: PointOnObject(g0,g-4)
    c: Coincident(g1,g2)
    c: Symmetric(g0,g1,g-2)
    c: DistanceX(g1,g1) = 6.5
FEATURE [PartDesign::Pocket] Pocket006  label="P-Adapter 10x20 raw"
  BaseFeature = -> Hole
  Direction = (1,0,0)
  Length = 25
  Length2 = 5
  Profile = -> Sketch048
  ReferenceAxis = -> Sketch048 [N_Axis]
  Refine = true
  Reversed = true
  Suppressed = false
  Type = 0
FEATURE [PartDesign::Chamfer] Chamfer004  label="P-Adapter 10x20 gefast"
  Angle = 45
  Base = -> Pocket006 [Edge45,Edge47,Edge49,Edge48,Edge9,Edge10,Edge7,Edge8]
  BaseFeature = -> Pocket006
  ChamferType = 0
  FlipDirection = false
  Refine = true
  Size = 0.5
  Size2 = 1
  SupportTransform = false
  Suppressed = false
  UseAllEdges = false
FEATURE [PartDesign::Body] Body019  label="B-Scherenheberwellenkupplung-10x20mm"
  AllowCompound = false
  Group = -> [Sketch037,Pad020,Sketch041,Pad022,Sketch042,Pocket005,Sketch044,Sketch045,SubtractiveLoft,Sketch046,Hole,Sketch048,Pocket006,Chamfer004]
  Origin = -> Origin009
  Placement = pos=(-151.6,-158.3,0) rot=(0,0,1;0rad)
  Tip = -> Chamfer004
FEATURE [App::DocumentObjectGroup] Group  label="Bodies"
  Group = -> [Body,Body001,Body012,Body004,Body005,Body008,Body010,Body014,Body015,Body019,Body021]
FEATURE [Part::Feature] Body023  label="P-Scherenheberwellenkupplung-10x20mm"
  Placement = pos=(-151.6,-158.3,0) rot=(0,0,1;0rad)
  shape: bbox 34 x 34 x 45.72 mm, 396 faces (baked)
FEATURE [App::DocumentObjectGroup] Group003  label="Solids"
  Group = -> [Body003,Body002,Body013,Body007,Body006,Body009,Body011,Body016,Body017,Body018,Body023,Body022]
FEATURE [Mesh::Feature] Mesh012  label="M-Scherenheberwellenkupplung-10x20mm"
FEATURE [App::DocumentObjectGroup] Group002  label="Meshes"
  Group = -> [Mesh,Mesh001,Mesh006,Mesh003,Mesh004,Mesh002,Mesh005,Mesh008,Mesh009,Mesh007,Mesh011,Mesh012]
